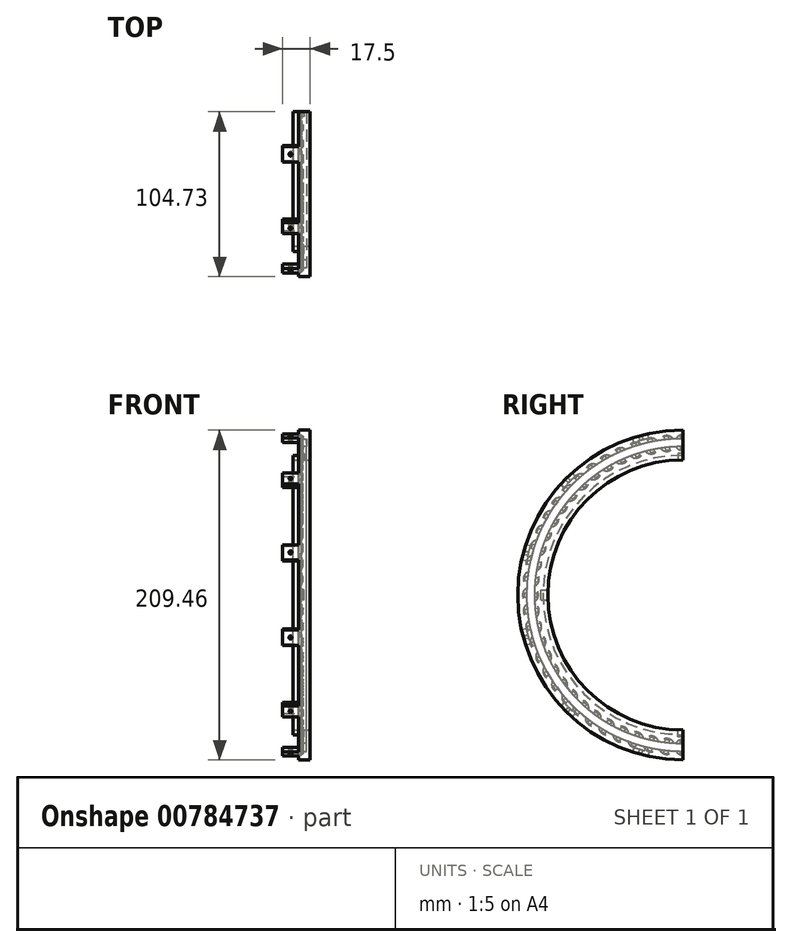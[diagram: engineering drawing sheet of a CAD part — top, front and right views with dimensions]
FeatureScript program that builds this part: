
annotation { "Feature Type Name" : "Feature", "Feature Type Description" : "" }
export const myFeature = defineFeature(function(context is Context, id is Id, definition is map)
    precondition{}
    {
        {
            var Q0;
            Q0=qCreatedBy(makeId("Front.planeOp"),FACE);
            var sketch = newSketch(context, id + "F0", { "sketchPlane" : qUnion([Q0])});
            skLineSegment(sketch, "E0.bottom", {"start": v(-125, 105) * mm, "end": v(125, 105) * mm, "construction": true});
            skLineSegment(sketch, "E0.top", {"start": v(-125, -105) * mm, "end": v(125, -105) * mm, "construction": true});
            skLineSegment(sketch, "E0.left", {"start": v(-125, 105) * mm, "end": v(-125, -105) * mm, "construction": true});
            skLineSegment(sketch, "E0.right", {"start": v(125, 105) * mm, "end": v(125, -105) * mm, "construction": true});
            skLineSegment(sketch, "E1", {"start": v(-16.75, 85.73) * mm, "end": v(-16.75, 88.73) * mm});
            skLineSegment(sketch, "E2", {"start": v(-16.75, 88.73) * mm, "end": v(-13.25, 88.73) * mm});
            skLineSegment(sketch, "E3", {"start": v(-16.75, 85.73) * mm, "end": v(-5.75, 85.73) * mm});
            skLineSegment(sketch, "E4", {"start": v(-5.75, 85.73) * mm, "end": v(-5.75, 104.73) * mm});
            skLineSegment(sketch, "E5", {"start": v(-13.25, 104.73) * mm, "end": v(-13.25, 99.23) * mm});
            skLineSegment(sketch, "E6", {"start": v(-13.25, 99.23) * mm, "end": v(-8.25, 99.23) * mm});
            skLineSegment(sketch, "E7", {"start": v(-8.25, 99.23) * mm, "end": v(-8.25, 94.23) * mm});
            skLineSegment(sketch, "E8", {"start": v(-8.25, 94.23) * mm, "end": v(-13.25, 94.23) * mm});
            skLineSegment(sketch, "E9.trimOffspring", {"start": v(-13.25, 94.23) * mm, "end": v(-13.25, 88.73) * mm});
            skLineSegment(sketch, "E10", {"start": v(-74.95, 0) * mm, "end": v(74.95, 0) * mm});
            skLineSegment(sketch, "E11", {"start": v(-13.25, 104.73) * mm, "end": v(-8.75, 104.73) * mm});
            skLineSegment(sketch, "E12.trimOffspring", {"start": v(-7.75, 104.73) * mm, "end": v(-5.75, 104.73) * mm});
            skLineSegment(sketch, "E13", {"start": v(-7.75, 104.73) * mm, "end": v(-8.75, 104.73) * mm});
            skSolve(sketch);
        }
        {
            var Q0;
            Q0 = qSketchRegion(id + "F0", true);
            var Q1;
            Q1=sQuery(id+"F0.wireOp",EDGE,"E10");
            revolve(context, id + "F1", {"surfaceOperationType" : NewSurfaceOperationType.NEW, "entities" : qUnion([Q0]), "axis" : qUnion([Q1]), "revolveType" : RevolveType.ONE_DIRECTION, "angle" : 180 * degree});
        }
        {
            var Q0;
            Q0=qCreatedBy(makeId("Top.planeOp"),FACE);
            cPlane(context, id + "F2", {"entities" : qUnion([Q0]), "cplaneType" : CPlaneType.OFFSET, "offset" : 80 * mm, "oppositeDirection" : true, "width" : 150 * mm, "height" : 150 * mm});
        }
        {
            var Q0;
            Q0=qCreatedBy(id+"F2.planeOp",FACE);
            var sketch = newSketch(context, id + "F3", { "sketchPlane" : qUnion([Q0])});
            skLineSegment(sketch, "E14.top", {"start": v(-9.65, -3.1) * mm, "end": v(-12.85, -3.1) * mm});
            skLineSegment(sketch, "E14.left", {"start": v(-9.65, 0) * mm, "end": v(-9.65, -3.1) * mm});
            skLineSegment(sketch, "E14.right", {"start": v(-12.85, 0) * mm, "end": v(-12.85, -3.1) * mm});
            skLineSegment(sketch, "E15.top", {"start": v(-9.65, 1.57) * mm, "end": v(-12.85, 1.57) * mm});
            skLineSegment(sketch, "E15.left", {"start": v(-9.65, 0) * mm, "end": v(-9.65, 1.57) * mm});
            skLineSegment(sketch, "E15.right", {"start": v(-12.85, 0) * mm, "end": v(-12.85, 1.57) * mm});
            skSolve(sketch);
        }
        {
            var Q0;
            Q0 = qSketchRegion(id + "F3", true);
            var Q1;
            Q1=makeQuery(id+"F1.opRevolve","SWEPT_FACE",FACE,{"disambiguationData":[OSD([sQuery(id+"F0.wireOp",EDGE,"E2")])]});
            extrude(context, id + "F4", {"entities" : qUnion([Q0]), "operationType" : NewBodyOperationType.REMOVE, "oppositeDirection" : true, "depth" : 10 * mm, "endBoundEntityFace" : qUnion([Q1]), "offsetDistance" : 25 * mm});
        }
        {
            var Q0;
            Q0=qCreatedBy(makeId("Front.planeOp"),FACE);
            cPlane(context, id + "F5", {"entities" : qUnion([Q0]), "cplaneType" : CPlaneType.OFFSET, "offset" : 80 * mm, "width" : 150 * mm, "height" : 150 * mm});
        }
        {
            var Q0;
            Q0=qCreatedBy(makeId("Top.planeOp"),FACE);
            cPlane(context, id + "F6", {"entities" : qUnion([Q0]), "cplaneType" : CPlaneType.OFFSET, "offset" : 80 * mm, "width" : 150 * mm, "height" : 150 * mm});
        }
        {
            var Q0;
            Q0=qCreatedBy(id+"F5.planeOp",FACE);
            var sketch = newSketch(context, id + "F7", { "sketchPlane" : qUnion([Q0])});
            skLineSegment(sketch, "E16.bottom", {"start": v(-9.65, -3.1) * mm, "end": v(-12.85, -3.1) * mm});
            skLineSegment(sketch, "E16.top", {"start": v(-9.65, 3.1) * mm, "end": v(-12.85, 3.1) * mm});
            skLineSegment(sketch, "E16.left", {"start": v(-9.65, -3.1) * mm, "end": v(-9.65, 3.1) * mm});
            skLineSegment(sketch, "E16.right", {"start": v(-12.85, -3.1) * mm, "end": v(-12.85, 3.1) * mm});
            skSolve(sketch);
        }
        {
            var Q0;
            Q0 = qSketchRegion(id + "F7", true);
            var Q1;
            Q1=makeQuery(id+"F1.opRevolve","SWEPT_FACE",FACE,{"disambiguationData":[OSD([sQuery(id+"F0.wireOp",EDGE,"E2")])]});
            extrude(context, id + "F8", {"entities" : qUnion([Q0]), "operationType" : NewBodyOperationType.REMOVE, "depth" : 10 * mm, "endBoundEntityFace" : qUnion([Q1]), "offsetDistance" : 25 * mm});
        }
        {
            var Q0;
            Q0=qCreatedBy(id+"F6.planeOp",FACE);
            var sketch = newSketch(context, id + "F9", { "sketchPlane" : qUnion([Q0])});
            skLineSegment(sketch, "E17.bottom", {"start": v(-9.65, 0) * mm, "end": v(-12.85, 0) * mm});
            skLineSegment(sketch, "E17.top", {"start": v(-9.65, -3.1) * mm, "end": v(-12.85, -3.1) * mm});
            skLineSegment(sketch, "E17.left", {"start": v(-9.65, 0) * mm, "end": v(-9.65, -3.1) * mm});
            skLineSegment(sketch, "E17.right", {"start": v(-12.85, 0) * mm, "end": v(-12.85, -3.1) * mm});
            skSolve(sketch);
        }
        {
            var Q0;
            Q0 = qSketchRegion(id + "F9", true);
            var Q1;
            Q1=makeQuery(id+"F1.opRevolve","SWEPT_FACE",FACE,{"disambiguationData":[OSD([sQuery(id+"F0.wireOp",EDGE,"E2")])]});
            extrude(context, id + "F10", {"entities" : qUnion([Q0]), "operationType" : NewBodyOperationType.REMOVE, "depth" : 10 * mm, "endBoundEntityFace" : qUnion([Q1]), "offsetDistance" : 25 * mm});
        }
        {
            var Q0;
            Q0=makeQuery(id+"F1.opRevolve","SWEPT_FACE",FACE,{"disambiguationData":[OSD([sQuery(id+"F0.wireOp",EDGE,"E7")])]});
            var sketch = newSketch(context, id + "F11", { "sketchPlane" : qUnion([Q0])});
            skCircle(sketch, "E18", {"center": v(0, 96.73) * mm, "radius": 5 * mm});
            skCircle(sketch, "E19.1.0", {"center": v(-10.11, 96.2) * mm, "radius": 5 * mm});
            skCircle(sketch, "E19.2.0", {"center": v(-20.11, 94.62) * mm, "radius": 5 * mm});
            skCircle(sketch, "E19.3.0", {"center": v(-29.9, 92) * mm, "radius": 5 * mm});
            skCircle(sketch, "E19.4.0", {"center": v(-39.34, 88.37) * mm, "radius": 5 * mm});
            skCircle(sketch, "E19.5.0", {"center": v(-48.36, 83.77) * mm, "radius": 5 * mm});
            skCircle(sketch, "E19.6.0", {"center": v(-56.86, 78.26) * mm, "radius": 5 * mm});
            skCircle(sketch, "E19.7.0", {"center": v(-64.73, 71.88) * mm, "radius": 5 * mm});
            skCircle(sketch, "E19.8.0", {"center": v(-71.88, 64.73) * mm, "radius": 5 * mm});
            skCircle(sketch, "E19.9.0", {"center": v(-78.26, 56.86) * mm, "radius": 5 * mm});
            skCircle(sketch, "E19.10.0", {"center": v(-83.77, 48.36) * mm, "radius": 5 * mm});
            skCircle(sketch, "E19.11.0", {"center": v(-88.37, 39.34) * mm, "radius": 5 * mm});
            skCircle(sketch, "E19.12.0", {"center": v(-92, 29.9) * mm, "radius": 5 * mm});
            skCircle(sketch, "E19.13.0", {"center": v(-94.62, 20.11) * mm, "radius": 5 * mm});
            skCircle(sketch, "E19.14.0", {"center": v(-96.2, 10.11) * mm, "radius": 5 * mm});
            skCircle(sketch, "E19.15.0", {"center": v(-96.73, 0) * mm, "radius": 5 * mm});
            skCircle(sketch, "E19.16.0", {"center": v(-96.2, -10.11) * mm, "radius": 5 * mm});
            skCircle(sketch, "E19.17.0", {"center": v(-94.62, -20.11) * mm, "radius": 5 * mm});
            skCircle(sketch, "E19.18.0", {"center": v(-92, -29.9) * mm, "radius": 5 * mm});
            skCircle(sketch, "E19.19.0", {"center": v(-88.37, -39.34) * mm, "radius": 5 * mm});
            skCircle(sketch, "E19.20.0", {"center": v(-83.77, -48.36) * mm, "radius": 5 * mm});
            skCircle(sketch, "E19.21.0", {"center": v(-78.26, -56.86) * mm, "radius": 5 * mm});
            skCircle(sketch, "E19.22.0", {"center": v(-71.88, -64.73) * mm, "radius": 5 * mm});
            skCircle(sketch, "E19.23.0", {"center": v(-64.73, -71.88) * mm, "radius": 5 * mm});
            skCircle(sketch, "E19.24.0", {"center": v(-56.86, -78.26) * mm, "radius": 5 * mm});
            skCircle(sketch, "E19.25.0", {"center": v(-48.36, -83.77) * mm, "radius": 5 * mm});
            skCircle(sketch, "E19.26.0", {"center": v(-39.34, -88.37) * mm, "radius": 5 * mm});
            skCircle(sketch, "E19.27.0", {"center": v(-29.9, -92) * mm, "radius": 5 * mm});
            skCircle(sketch, "E19.28.0", {"center": v(-20.11, -94.62) * mm, "radius": 5 * mm});
            skCircle(sketch, "E19.29.0", {"center": v(-10.11, -96.2) * mm, "radius": 5 * mm});
            skCircle(sketch, "E19.30.0", {"center": v(0, -96.73) * mm, "radius": 5 * mm});
            skCircle(sketch, "E19.31.0", {"center": v(10.11, -96.2) * mm, "radius": 5 * mm});
            skCircle(sketch, "E19.32.0", {"center": v(20.11, -94.62) * mm, "radius": 5 * mm});
            skCircle(sketch, "E19.33.0", {"center": v(29.9, -92) * mm, "radius": 5 * mm});
            skCircle(sketch, "E19.34.0", {"center": v(39.34, -88.37) * mm, "radius": 5 * mm});
            skCircle(sketch, "E19.35.0", {"center": v(48.36, -83.77) * mm, "radius": 5 * mm});
            skCircle(sketch, "E19.36.0", {"center": v(56.86, -78.26) * mm, "radius": 5 * mm});
            skCircle(sketch, "E19.37.0", {"center": v(64.73, -71.88) * mm, "radius": 5 * mm});
            skCircle(sketch, "E19.38.0", {"center": v(71.88, -64.73) * mm, "radius": 5 * mm});
            skCircle(sketch, "E19.39.0", {"center": v(78.26, -56.86) * mm, "radius": 5 * mm});
            skCircle(sketch, "E19.40.0", {"center": v(83.77, -48.37) * mm, "radius": 5 * mm});
            skCircle(sketch, "E19.41.0", {"center": v(88.37, -39.34) * mm, "radius": 5 * mm});
            skCircle(sketch, "E19.42.0", {"center": v(92, -29.9) * mm, "radius": 5 * mm});
            skCircle(sketch, "E19.43.0", {"center": v(94.62, -20.11) * mm, "radius": 5 * mm});
            skCircle(sketch, "E19.44.0", {"center": v(96.2, -10.11) * mm, "radius": 5 * mm});
            skCircle(sketch, "E19.45.0", {"center": v(96.73, 0) * mm, "radius": 5 * mm});
            skCircle(sketch, "E19.46.0", {"center": v(96.2, 10.11) * mm, "radius": 5 * mm});
            skCircle(sketch, "E19.47.0", {"center": v(94.62, 20.11) * mm, "radius": 5 * mm});
            skCircle(sketch, "E19.48.0", {"center": v(92, 29.9) * mm, "radius": 5 * mm});
            skCircle(sketch, "E19.49.0", {"center": v(88.37, 39.34) * mm, "radius": 5 * mm});
            skCircle(sketch, "E19.50.0", {"center": v(83.77, 48.36) * mm, "radius": 5 * mm});
            skCircle(sketch, "E19.51.0", {"center": v(78.26, 56.86) * mm, "radius": 5 * mm});
            skCircle(sketch, "E19.52.0", {"center": v(71.88, 64.73) * mm, "radius": 5 * mm});
            skCircle(sketch, "E19.53.0", {"center": v(64.73, 71.88) * mm, "radius": 5 * mm});
            skCircle(sketch, "E19.54.0", {"center": v(56.86, 78.26) * mm, "radius": 5 * mm});
            skCircle(sketch, "E19.55.0", {"center": v(48.36, 83.77) * mm, "radius": 5 * mm});
            skCircle(sketch, "E19.56.0", {"center": v(39.34, 88.37) * mm, "radius": 5 * mm});
            skCircle(sketch, "E19.57.0", {"center": v(29.9, 92) * mm, "radius": 5 * mm});
            skCircle(sketch, "E19.58.0", {"center": v(20.11, 94.62) * mm, "radius": 5 * mm});
            skCircle(sketch, "E19.59.0", {"center": v(10.11, 96.2) * mm, "radius": 5 * mm});
            skPoint(sketch, "E19.center", {"position": v(0, 0) * mm});
            skSolve(sketch);
        }
        {
            var Q0;
            Q0 = qSketchRegion(id + "F11", true);
            extrude(context, id + "F12", {"entities" : qUnion([Q0]), "operationType" : NewBodyOperationType.REMOVE, "depth" : 25 * mm, "offsetDistance" : 25 * mm, "hasSecondDirection" : true, "secondDirectionOppositeDirection" : false, "secondDirectionDepth" : 3 * mm});
        }
        {
            var Q0;
            Q0=makeQuery(id+"F1.opRevolve","SWEPT_FACE",FACE,{"disambiguationData":[OSD([sQuery(id+"F0.wireOp",EDGE,"E7")])]});
            var sketch = newSketch(context, id + "F13", { "sketchPlane" : qUnion([Q0])});
            skLineSegment(sketch, "E20.bottom", {"start": v(1.36, 92.48) * mm, "end": v(0, 92.48) * mm});
            skLineSegment(sketch, "E20.top", {"start": v(1.36, 100.98) * mm, "end": v(0, 100.98) * mm});
            skLineSegment(sketch, "E20.left", {"start": v(1.36, 92.48) * mm, "end": v(1.36, 100.98) * mm});
            skLineSegment(sketch, "E21", {"start": v(1.96, 96.73) * mm, "end": v(-1.46, 96.73) * mm, "construction": true});
            skLineSegment(sketch, "E22.MirrorCS", {"start": v(-1.36, 92.48) * mm, "end": v(0, 92.48) * mm});
            skLineSegment(sketch, "E23.MirrorCS", {"start": v(-1.36, 92.48) * mm, "end": v(-1.36, 100.98) * mm});
            skLineSegment(sketch, "E24.MirrorCS", {"start": v(-1.36, 100.98) * mm, "end": v(0, 100.98) * mm});
            skLineSegment(sketch, "E25", {"start": v(0, 92.48) * mm, "end": v(0, 100.98) * mm, "construction": true});
            skLineSegment(sketch, "E26.1.0", {"start": v(-8.32, 92.12) * mm, "end": v(-9.67, 91.97) * mm});
            skLineSegment(sketch, "E26.1.1", {"start": v(-9.2, 100.57) * mm, "end": v(-10.56, 100.43) * mm});
            skLineSegment(sketch, "E26.1.2", {"start": v(-8.32, 92.12) * mm, "end": v(-9.2, 100.57) * mm});
            skLineSegment(sketch, "E26.1.3", {"start": v(-8.16, 96.4) * mm, "end": v(-11.56, 96.05) * mm, "construction": true});
            skLineSegment(sketch, "E26.1.4", {"start": v(-11.02, 91.83) * mm, "end": v(-9.67, 91.97) * mm});
            skLineSegment(sketch, "E26.1.5", {"start": v(-11.02, 91.83) * mm, "end": v(-11.9, 100.28) * mm});
            skLineSegment(sketch, "E26.1.6", {"start": v(-11.9, 100.28) * mm, "end": v(-10.56, 100.43) * mm});
            skLineSegment(sketch, "E26.1.7", {"start": v(-9.67, 91.97) * mm, "end": v(-10.56, 100.43) * mm, "construction": true});
            skLineSegment(sketch, "E26.2.0", {"start": v(-17.9, 90.74) * mm, "end": v(-19.23, 90.46) * mm});
            skLineSegment(sketch, "E26.2.1", {"start": v(-19.67, 99.06) * mm, "end": v(-21, 98.77) * mm});
            skLineSegment(sketch, "E26.2.2", {"start": v(-17.9, 90.74) * mm, "end": v(-19.67, 99.06) * mm});
            skLineSegment(sketch, "E26.2.3", {"start": v(-18.2, 95.02) * mm, "end": v(-21.54, 94.31) * mm, "construction": true});
            skLineSegment(sketch, "E26.2.4", {"start": v(-20.56, 90.18) * mm, "end": v(-19.23, 90.46) * mm});
            skLineSegment(sketch, "E26.2.5", {"start": v(-20.56, 90.18) * mm, "end": v(-22.32, 98.5) * mm});
            skLineSegment(sketch, "E26.2.6", {"start": v(-22.32, 98.5) * mm, "end": v(-21, 98.77) * mm});
            skLineSegment(sketch, "E26.2.7", {"start": v(-19.23, 90.46) * mm, "end": v(-21, 98.77) * mm, "construction": true});
            skLineSegment(sketch, "E26.3.0", {"start": v(-27.29, 88.37) * mm, "end": v(-28.58, 87.95) * mm});
            skLineSegment(sketch, "E26.3.1", {"start": v(-29.91, 96.46) * mm, "end": v(-31.2, 96.04) * mm});
            skLineSegment(sketch, "E26.3.2", {"start": v(-27.29, 88.37) * mm, "end": v(-29.91, 96.46) * mm});
            skLineSegment(sketch, "E26.3.3", {"start": v(-28.02, 92.6) * mm, "end": v(-31.28, 91.54) * mm, "construction": true});
            skLineSegment(sketch, "E26.3.4", {"start": v(-29.87, 87.53) * mm, "end": v(-28.58, 87.95) * mm});
            skLineSegment(sketch, "E26.3.5", {"start": v(-29.87, 87.53) * mm, "end": v(-32.5, 95.62) * mm});
            skLineSegment(sketch, "E26.3.6", {"start": v(-32.5, 95.62) * mm, "end": v(-31.2, 96.04) * mm});
            skLineSegment(sketch, "E26.3.7", {"start": v(-28.58, 87.95) * mm, "end": v(-31.2, 96.04) * mm, "construction": true});
            skLineSegment(sketch, "E26.4.0", {"start": v(-36.37, 85.04) * mm, "end": v(-37.62, 84.48) * mm});
            skLineSegment(sketch, "E26.4.1", {"start": v(-39.83, 92.8) * mm, "end": v(-41.07, 92.25) * mm});
            skLineSegment(sketch, "E26.4.2", {"start": v(-36.37, 85.04) * mm, "end": v(-39.83, 92.8) * mm});
            skLineSegment(sketch, "E26.4.3", {"start": v(-37.55, 89.17) * mm, "end": v(-40.68, 87.77) * mm, "construction": true});
            skLineSegment(sketch, "E26.4.4", {"start": v(-38.86, 83.93) * mm, "end": v(-37.62, 84.48) * mm});
            skLineSegment(sketch, "E26.4.5", {"start": v(-38.86, 83.93) * mm, "end": v(-42.31, 91.7) * mm});
            skLineSegment(sketch, "E26.4.6", {"start": v(-42.31, 91.7) * mm, "end": v(-41.07, 92.25) * mm});
            skLineSegment(sketch, "E26.4.7", {"start": v(-37.62, 84.48) * mm, "end": v(-41.07, 92.25) * mm, "construction": true});
            skLineSegment(sketch, "E26.5.0", {"start": v(-45.06, 80.77) * mm, "end": v(-46.24, 80.1) * mm});
            skLineSegment(sketch, "E26.5.1", {"start": v(-49.31, 88.13) * mm, "end": v(-50.49, 87.45) * mm});
            skLineSegment(sketch, "E26.5.2", {"start": v(-45.06, 80.77) * mm, "end": v(-49.31, 88.13) * mm});
            skLineSegment(sketch, "E26.5.3", {"start": v(-46.67, 84.75) * mm, "end": v(-49.63, 83.04) * mm, "construction": true});
            skLineSegment(sketch, "E26.5.4", {"start": v(-47.42, 79.41) * mm, "end": v(-46.24, 80.1) * mm});
            skLineSegment(sketch, "E26.5.5", {"start": v(-47.42, 79.41) * mm, "end": v(-51.67, 86.77) * mm});
            skLineSegment(sketch, "E26.5.6", {"start": v(-51.67, 86.77) * mm, "end": v(-50.49, 87.45) * mm});
            skLineSegment(sketch, "E26.5.7", {"start": v(-46.24, 80.1) * mm, "end": v(-50.49, 87.45) * mm, "construction": true});
            skLineSegment(sketch, "E26.6.0", {"start": v(-53.26, 75.62) * mm, "end": v(-54.36, 74.82) * mm});
            skLineSegment(sketch, "E26.6.1", {"start": v(-58.26, 82.5) * mm, "end": v(-59.35, 81.7) * mm});
            skLineSegment(sketch, "E26.6.2", {"start": v(-53.26, 75.62) * mm, "end": v(-58.26, 82.5) * mm});
            skLineSegment(sketch, "E26.6.3", {"start": v(-55.27, 79.4) * mm, "end": v(-58.04, 77.4) * mm, "construction": true});
            skLineSegment(sketch, "E26.6.4", {"start": v(-55.46, 74.02) * mm, "end": v(-54.36, 74.82) * mm});
            skLineSegment(sketch, "E26.6.5", {"start": v(-55.46, 74.02) * mm, "end": v(-60.45, 80.9) * mm});
            skLineSegment(sketch, "E26.6.6", {"start": v(-60.45, 80.9) * mm, "end": v(-59.35, 81.7) * mm});
            skLineSegment(sketch, "E26.6.7", {"start": v(-54.36, 74.82) * mm, "end": v(-59.35, 81.7) * mm, "construction": true});
            skLineSegment(sketch, "E26.7.0", {"start": v(-60.87, 69.63) * mm, "end": v(-61.88, 68.73) * mm});
            skLineSegment(sketch, "E26.7.1", {"start": v(-66.56, 75.95) * mm, "end": v(-67.57, 75.04) * mm});
            skLineSegment(sketch, "E26.7.2", {"start": v(-60.87, 69.63) * mm, "end": v(-66.56, 75.95) * mm});
            skLineSegment(sketch, "E26.7.3", {"start": v(-63.27, 73.2) * mm, "end": v(-65.8, 70.9) * mm, "construction": true});
            skLineSegment(sketch, "E26.7.4", {"start": v(-62.9, 67.82) * mm, "end": v(-61.88, 68.73) * mm});
            skLineSegment(sketch, "E26.7.5", {"start": v(-62.9, 67.82) * mm, "end": v(-68.58, 74.13) * mm});
            skLineSegment(sketch, "E26.7.6", {"start": v(-68.58, 74.13) * mm, "end": v(-67.57, 75.04) * mm});
            skLineSegment(sketch, "E26.7.7", {"start": v(-61.88, 68.73) * mm, "end": v(-67.57, 75.04) * mm, "construction": true});
            skLineSegment(sketch, "E26.8.0", {"start": v(-67.82, 62.9) * mm, "end": v(-68.73, 61.88) * mm});
            skLineSegment(sketch, "E26.8.1", {"start": v(-74.13, 68.58) * mm, "end": v(-75.04, 67.57) * mm});
            skLineSegment(sketch, "E26.8.2", {"start": v(-67.82, 62.9) * mm, "end": v(-74.13, 68.58) * mm});
            skLineSegment(sketch, "E26.8.3", {"start": v(-70.57, 66.18) * mm, "end": v(-72.86, 63.64) * mm, "construction": true});
            skLineSegment(sketch, "E26.8.4", {"start": v(-69.63, 60.87) * mm, "end": v(-68.73, 61.88) * mm});
            skLineSegment(sketch, "E26.8.5", {"start": v(-69.63, 60.87) * mm, "end": v(-75.95, 66.56) * mm});
            skLineSegment(sketch, "E26.8.6", {"start": v(-75.95, 66.56) * mm, "end": v(-75.04, 67.57) * mm});
            skLineSegment(sketch, "E26.8.7", {"start": v(-68.73, 61.88) * mm, "end": v(-75.04, 67.57) * mm, "construction": true});
            skLineSegment(sketch, "E26.9.0", {"start": v(-74.02, 55.46) * mm, "end": v(-74.82, 54.36) * mm});
            skLineSegment(sketch, "E26.9.1", {"start": v(-80.9, 60.45) * mm, "end": v(-81.7, 59.35) * mm});
            skLineSegment(sketch, "E26.9.2", {"start": v(-74.02, 55.46) * mm, "end": v(-80.9, 60.45) * mm});
            skLineSegment(sketch, "E26.9.3", {"start": v(-77.1, 58.44) * mm, "end": v(-79.11, 55.68) * mm, "construction": true});
            skLineSegment(sketch, "E26.9.4", {"start": v(-75.62, 53.26) * mm, "end": v(-74.82, 54.36) * mm});
            skLineSegment(sketch, "E26.9.5", {"start": v(-75.62, 53.26) * mm, "end": v(-82.5, 58.26) * mm});
            skLineSegment(sketch, "E26.9.6", {"start": v(-82.5, 58.26) * mm, "end": v(-81.7, 59.35) * mm});
            skLineSegment(sketch, "E26.9.7", {"start": v(-74.82, 54.36) * mm, "end": v(-81.7, 59.35) * mm, "construction": true});
            skLineSegment(sketch, "E26.10.0", {"start": v(-79.41, 47.42) * mm, "end": v(-80.1, 46.24) * mm});
            skLineSegment(sketch, "E26.10.1", {"start": v(-86.77, 51.67) * mm, "end": v(-87.45, 50.49) * mm});
            skLineSegment(sketch, "E26.10.2", {"start": v(-79.41, 47.42) * mm, "end": v(-86.77, 51.67) * mm});
            skLineSegment(sketch, "E26.10.3", {"start": v(-82.79, 50.06) * mm, "end": v(-84.5, 47.1) * mm, "construction": true});
            skLineSegment(sketch, "E26.10.4", {"start": v(-80.77, 45.06) * mm, "end": v(-80.1, 46.24) * mm});
            skLineSegment(sketch, "E26.10.5", {"start": v(-80.77, 45.06) * mm, "end": v(-88.13, 49.31) * mm});
            skLineSegment(sketch, "E26.10.6", {"start": v(-88.13, 49.31) * mm, "end": v(-87.45, 50.49) * mm});
            skLineSegment(sketch, "E26.10.7", {"start": v(-80.1, 46.24) * mm, "end": v(-87.45, 50.49) * mm, "construction": true});
            skLineSegment(sketch, "E26.11.0", {"start": v(-83.93, 38.86) * mm, "end": v(-84.48, 37.62) * mm});
            skLineSegment(sketch, "E26.11.1", {"start": v(-91.7, 42.31) * mm, "end": v(-92.25, 41.07) * mm});
            skLineSegment(sketch, "E26.11.2", {"start": v(-83.93, 38.86) * mm, "end": v(-91.7, 42.31) * mm});
            skLineSegment(sketch, "E26.11.3", {"start": v(-87.57, 41.14) * mm, "end": v(-88.96, 38) * mm, "construction": true});
            skLineSegment(sketch, "E26.11.4", {"start": v(-85.04, 36.37) * mm, "end": v(-84.48, 37.62) * mm});
            skLineSegment(sketch, "E26.11.5", {"start": v(-85.04, 36.37) * mm, "end": v(-92.8, 39.83) * mm});
            skLineSegment(sketch, "E26.11.6", {"start": v(-92.8, 39.83) * mm, "end": v(-92.25, 41.07) * mm});
            skLineSegment(sketch, "E26.11.7", {"start": v(-84.48, 37.62) * mm, "end": v(-92.25, 41.07) * mm, "construction": true});
            skLineSegment(sketch, "E26.12.0", {"start": v(-87.53, 29.87) * mm, "end": v(-87.95, 28.58) * mm});
            skLineSegment(sketch, "E26.12.1", {"start": v(-95.62, 32.5) * mm, "end": v(-96.04, 31.2) * mm});
            skLineSegment(sketch, "E26.12.2", {"start": v(-87.53, 29.87) * mm, "end": v(-95.62, 32.5) * mm});
            skLineSegment(sketch, "E26.12.3", {"start": v(-91.39, 31.76) * mm, "end": v(-92.45, 28.5) * mm, "construction": true});
            skLineSegment(sketch, "E26.12.4", {"start": v(-88.37, 27.29) * mm, "end": v(-87.95, 28.58) * mm});
            skLineSegment(sketch, "E26.12.5", {"start": v(-88.37, 27.29) * mm, "end": v(-96.46, 29.91) * mm});
            skLineSegment(sketch, "E26.12.6", {"start": v(-96.46, 29.91) * mm, "end": v(-96.04, 31.2) * mm});
            skLineSegment(sketch, "E26.12.7", {"start": v(-87.95, 28.58) * mm, "end": v(-96.04, 31.2) * mm, "construction": true});
            skLineSegment(sketch, "E26.13.0", {"start": v(-90.18, 20.56) * mm, "end": v(-90.46, 19.23) * mm});
            skLineSegment(sketch, "E26.13.1", {"start": v(-98.5, 22.32) * mm, "end": v(-98.77, 21) * mm});
            skLineSegment(sketch, "E26.13.2", {"start": v(-90.18, 20.56) * mm, "end": v(-98.5, 22.32) * mm});
            skLineSegment(sketch, "E26.13.3", {"start": v(-94.2, 22.03) * mm, "end": v(-94.92, 18.68) * mm, "construction": true});
            skLineSegment(sketch, "E26.13.4", {"start": v(-90.74, 17.9) * mm, "end": v(-90.46, 19.23) * mm});
            skLineSegment(sketch, "E26.13.5", {"start": v(-90.74, 17.9) * mm, "end": v(-99.06, 19.67) * mm});
            skLineSegment(sketch, "E26.13.6", {"start": v(-99.06, 19.67) * mm, "end": v(-98.77, 21) * mm});
            skLineSegment(sketch, "E26.13.7", {"start": v(-90.46, 19.23) * mm, "end": v(-98.77, 21) * mm, "construction": true});
            skLineSegment(sketch, "E26.14.0", {"start": v(-91.83, 11.02) * mm, "end": v(-91.97, 9.67) * mm});
            skLineSegment(sketch, "E26.14.1", {"start": v(-100.28, 11.9) * mm, "end": v(-100.43, 10.56) * mm});
            skLineSegment(sketch, "E26.14.2", {"start": v(-91.83, 11.02) * mm, "end": v(-100.28, 11.9) * mm});
            skLineSegment(sketch, "E26.14.3", {"start": v(-96, 12.06) * mm, "end": v(-96.35, 8.66) * mm, "construction": true});
            skLineSegment(sketch, "E26.14.4", {"start": v(-92.12, 8.32) * mm, "end": v(-91.97, 9.67) * mm});
            skLineSegment(sketch, "E26.14.5", {"start": v(-92.12, 8.32) * mm, "end": v(-100.57, 9.2) * mm});
            skLineSegment(sketch, "E26.14.6", {"start": v(-100.57, 9.2) * mm, "end": v(-100.43, 10.56) * mm});
            skLineSegment(sketch, "E26.14.7", {"start": v(-91.97, 9.67) * mm, "end": v(-100.43, 10.56) * mm, "construction": true});
            skLineSegment(sketch, "E26.15.0", {"start": v(-92.48, 1.36) * mm, "end": v(-92.48, 0) * mm});
            skLineSegment(sketch, "E26.15.1", {"start": v(-100.98, 1.36) * mm, "end": v(-100.98, 0) * mm});
            skLineSegment(sketch, "E26.15.2", {"start": v(-92.48, 1.36) * mm, "end": v(-100.98, 1.36) * mm});
            skLineSegment(sketch, "E26.15.3", {"start": v(-96.73, 1.96) * mm, "end": v(-96.73, -1.46) * mm, "construction": true});
            skLineSegment(sketch, "E26.15.4", {"start": v(-92.48, -1.36) * mm, "end": v(-92.48, 0) * mm});
            skLineSegment(sketch, "E26.15.5", {"start": v(-92.48, -1.36) * mm, "end": v(-100.98, -1.36) * mm});
            skLineSegment(sketch, "E26.15.6", {"start": v(-100.98, -1.36) * mm, "end": v(-100.98, 0) * mm});
            skLineSegment(sketch, "E26.15.7", {"start": v(-92.48, 0) * mm, "end": v(-100.98, 0) * mm, "construction": true});
            skLineSegment(sketch, "E26.16.0", {"start": v(-92.12, -8.32) * mm, "end": v(-91.97, -9.67) * mm});
            skLineSegment(sketch, "E26.16.1", {"start": v(-100.57, -9.2) * mm, "end": v(-100.43, -10.56) * mm});
            skLineSegment(sketch, "E26.16.2", {"start": v(-92.12, -8.32) * mm, "end": v(-100.57, -9.2) * mm});
            skLineSegment(sketch, "E26.16.3", {"start": v(-96.4, -8.16) * mm, "end": v(-96.05, -11.56) * mm, "construction": true});
            skLineSegment(sketch, "E26.16.4", {"start": v(-91.83, -11.02) * mm, "end": v(-91.97, -9.67) * mm});
            skLineSegment(sketch, "E26.16.5", {"start": v(-91.83, -11.02) * mm, "end": v(-100.28, -11.9) * mm});
            skLineSegment(sketch, "E26.16.6", {"start": v(-100.28, -11.9) * mm, "end": v(-100.43, -10.56) * mm});
            skLineSegment(sketch, "E26.16.7", {"start": v(-91.97, -9.67) * mm, "end": v(-100.43, -10.56) * mm, "construction": true});
            skLineSegment(sketch, "E26.17.0", {"start": v(-90.74, -17.9) * mm, "end": v(-90.46, -19.23) * mm});
            skLineSegment(sketch, "E26.17.1", {"start": v(-99.06, -19.67) * mm, "end": v(-98.77, -21) * mm});
            skLineSegment(sketch, "E26.17.2", {"start": v(-90.74, -17.9) * mm, "end": v(-99.06, -19.67) * mm});
            skLineSegment(sketch, "E26.17.3", {"start": v(-95.02, -18.2) * mm, "end": v(-94.31, -21.54) * mm, "construction": true});
            skLineSegment(sketch, "E26.17.4", {"start": v(-90.18, -20.56) * mm, "end": v(-90.46, -19.23) * mm});
            skLineSegment(sketch, "E26.17.5", {"start": v(-90.18, -20.56) * mm, "end": v(-98.5, -22.32) * mm});
            skLineSegment(sketch, "E26.17.6", {"start": v(-98.5, -22.32) * mm, "end": v(-98.77, -21) * mm});
            skLineSegment(sketch, "E26.17.7", {"start": v(-90.46, -19.23) * mm, "end": v(-98.77, -21) * mm, "construction": true});
            skLineSegment(sketch, "E26.18.0", {"start": v(-88.37, -27.29) * mm, "end": v(-87.95, -28.58) * mm});
            skLineSegment(sketch, "E26.18.1", {"start": v(-96.46, -29.91) * mm, "end": v(-96.04, -31.2) * mm});
            skLineSegment(sketch, "E26.18.2", {"start": v(-88.37, -27.29) * mm, "end": v(-96.46, -29.91) * mm});
            skLineSegment(sketch, "E26.18.3", {"start": v(-92.6, -28.02) * mm, "end": v(-91.54, -31.28) * mm, "construction": true});
            skLineSegment(sketch, "E26.18.4", {"start": v(-87.53, -29.87) * mm, "end": v(-87.95, -28.58) * mm});
            skLineSegment(sketch, "E26.18.5", {"start": v(-87.53, -29.87) * mm, "end": v(-95.62, -32.5) * mm});
            skLineSegment(sketch, "E26.18.6", {"start": v(-95.62, -32.5) * mm, "end": v(-96.04, -31.2) * mm});
            skLineSegment(sketch, "E26.18.7", {"start": v(-87.95, -28.58) * mm, "end": v(-96.04, -31.2) * mm, "construction": true});
            skLineSegment(sketch, "E26.19.0", {"start": v(-85.04, -36.37) * mm, "end": v(-84.48, -37.62) * mm});
            skLineSegment(sketch, "E26.19.1", {"start": v(-92.8, -39.83) * mm, "end": v(-92.25, -41.07) * mm});
            skLineSegment(sketch, "E26.19.2", {"start": v(-85.04, -36.37) * mm, "end": v(-92.8, -39.83) * mm});
            skLineSegment(sketch, "E26.19.3", {"start": v(-89.17, -37.55) * mm, "end": v(-87.77, -40.68) * mm, "construction": true});
            skLineSegment(sketch, "E26.19.4", {"start": v(-83.93, -38.86) * mm, "end": v(-84.48, -37.62) * mm});
            skLineSegment(sketch, "E26.19.5", {"start": v(-83.93, -38.86) * mm, "end": v(-91.7, -42.31) * mm});
            skLineSegment(sketch, "E26.19.6", {"start": v(-91.7, -42.31) * mm, "end": v(-92.25, -41.07) * mm});
            skLineSegment(sketch, "E26.19.7", {"start": v(-84.48, -37.62) * mm, "end": v(-92.25, -41.07) * mm, "construction": true});
            skLineSegment(sketch, "E26.20.0", {"start": v(-80.77, -45.06) * mm, "end": v(-80.1, -46.24) * mm});
            skLineSegment(sketch, "E26.20.1", {"start": v(-88.13, -49.31) * mm, "end": v(-87.45, -50.49) * mm});
            skLineSegment(sketch, "E26.20.2", {"start": v(-80.77, -45.06) * mm, "end": v(-88.13, -49.31) * mm});
            skLineSegment(sketch, "E26.20.3", {"start": v(-84.75, -46.67) * mm, "end": v(-83.04, -49.63) * mm, "construction": true});
            skLineSegment(sketch, "E26.20.4", {"start": v(-79.41, -47.42) * mm, "end": v(-80.1, -46.24) * mm});
            skLineSegment(sketch, "E26.20.5", {"start": v(-79.41, -47.42) * mm, "end": v(-86.77, -51.67) * mm});
            skLineSegment(sketch, "E26.20.6", {"start": v(-86.77, -51.67) * mm, "end": v(-87.45, -50.49) * mm});
            skLineSegment(sketch, "E26.20.7", {"start": v(-80.1, -46.24) * mm, "end": v(-87.45, -50.49) * mm, "construction": true});
            skLineSegment(sketch, "E26.21.0", {"start": v(-75.62, -53.26) * mm, "end": v(-74.82, -54.36) * mm});
            skLineSegment(sketch, "E26.21.1", {"start": v(-82.5, -58.26) * mm, "end": v(-81.7, -59.35) * mm});
            skLineSegment(sketch, "E26.21.2", {"start": v(-75.62, -53.26) * mm, "end": v(-82.5, -58.26) * mm});
            skLineSegment(sketch, "E26.21.3", {"start": v(-79.4, -55.27) * mm, "end": v(-77.4, -58.04) * mm, "construction": true});
            skLineSegment(sketch, "E26.21.4", {"start": v(-74.02, -55.46) * mm, "end": v(-74.82, -54.36) * mm});
            skLineSegment(sketch, "E26.21.5", {"start": v(-74.02, -55.46) * mm, "end": v(-80.9, -60.45) * mm});
            skLineSegment(sketch, "E26.21.6", {"start": v(-80.9, -60.45) * mm, "end": v(-81.7, -59.35) * mm});
            skLineSegment(sketch, "E26.21.7", {"start": v(-74.82, -54.36) * mm, "end": v(-81.7, -59.35) * mm, "construction": true});
            skLineSegment(sketch, "E26.22.0", {"start": v(-69.63, -60.87) * mm, "end": v(-68.73, -61.88) * mm});
            skLineSegment(sketch, "E26.22.1", {"start": v(-75.95, -66.56) * mm, "end": v(-75.04, -67.57) * mm});
            skLineSegment(sketch, "E26.22.2", {"start": v(-69.63, -60.87) * mm, "end": v(-75.95, -66.56) * mm});
            skLineSegment(sketch, "E26.22.3", {"start": v(-73.2, -63.27) * mm, "end": v(-70.9, -65.8) * mm, "construction": true});
            skLineSegment(sketch, "E26.22.4", {"start": v(-67.82, -62.9) * mm, "end": v(-68.73, -61.88) * mm});
            skLineSegment(sketch, "E26.22.5", {"start": v(-67.82, -62.9) * mm, "end": v(-74.13, -68.58) * mm});
            skLineSegment(sketch, "E26.22.6", {"start": v(-74.13, -68.58) * mm, "end": v(-75.04, -67.57) * mm});
            skLineSegment(sketch, "E26.22.7", {"start": v(-68.73, -61.88) * mm, "end": v(-75.04, -67.57) * mm, "construction": true});
            skLineSegment(sketch, "E26.23.0", {"start": v(-62.9, -67.82) * mm, "end": v(-61.88, -68.73) * mm});
            skLineSegment(sketch, "E26.23.1", {"start": v(-68.58, -74.13) * mm, "end": v(-67.57, -75.04) * mm});
            skLineSegment(sketch, "E26.23.2", {"start": v(-62.9, -67.82) * mm, "end": v(-68.58, -74.13) * mm});
            skLineSegment(sketch, "E26.23.3", {"start": v(-66.18, -70.57) * mm, "end": v(-63.64, -72.86) * mm, "construction": true});
            skLineSegment(sketch, "E26.23.4", {"start": v(-60.87, -69.63) * mm, "end": v(-61.88, -68.73) * mm});
            skLineSegment(sketch, "E26.23.5", {"start": v(-60.87, -69.63) * mm, "end": v(-66.56, -75.95) * mm});
            skLineSegment(sketch, "E26.23.6", {"start": v(-66.56, -75.95) * mm, "end": v(-67.57, -75.04) * mm});
            skLineSegment(sketch, "E26.23.7", {"start": v(-61.88, -68.73) * mm, "end": v(-67.57, -75.04) * mm, "construction": true});
            skLineSegment(sketch, "E26.24.0", {"start": v(-55.46, -74.02) * mm, "end": v(-54.36, -74.82) * mm});
            skLineSegment(sketch, "E26.24.1", {"start": v(-60.45, -80.9) * mm, "end": v(-59.35, -81.7) * mm});
            skLineSegment(sketch, "E26.24.2", {"start": v(-55.46, -74.02) * mm, "end": v(-60.45, -80.9) * mm});
            skLineSegment(sketch, "E26.24.3", {"start": v(-58.44, -77.1) * mm, "end": v(-55.68, -79.11) * mm, "construction": true});
            skLineSegment(sketch, "E26.24.4", {"start": v(-53.26, -75.62) * mm, "end": v(-54.36, -74.82) * mm});
            skLineSegment(sketch, "E26.24.5", {"start": v(-53.26, -75.62) * mm, "end": v(-58.26, -82.5) * mm});
            skLineSegment(sketch, "E26.24.6", {"start": v(-58.26, -82.5) * mm, "end": v(-59.35, -81.7) * mm});
            skLineSegment(sketch, "E26.24.7", {"start": v(-54.36, -74.82) * mm, "end": v(-59.35, -81.7) * mm, "construction": true});
            skLineSegment(sketch, "E26.25.0", {"start": v(-47.42, -79.41) * mm, "end": v(-46.24, -80.1) * mm});
            skLineSegment(sketch, "E26.25.1", {"start": v(-51.67, -86.77) * mm, "end": v(-50.49, -87.45) * mm});
            skLineSegment(sketch, "E26.25.2", {"start": v(-47.42, -79.41) * mm, "end": v(-51.67, -86.77) * mm});
            skLineSegment(sketch, "E26.25.3", {"start": v(-50.06, -82.79) * mm, "end": v(-47.1, -84.5) * mm, "construction": true});
            skLineSegment(sketch, "E26.25.4", {"start": v(-45.06, -80.77) * mm, "end": v(-46.24, -80.1) * mm});
            skLineSegment(sketch, "E26.25.5", {"start": v(-45.06, -80.77) * mm, "end": v(-49.31, -88.13) * mm});
            skLineSegment(sketch, "E26.25.6", {"start": v(-49.31, -88.13) * mm, "end": v(-50.49, -87.45) * mm});
            skLineSegment(sketch, "E26.25.7", {"start": v(-46.24, -80.1) * mm, "end": v(-50.49, -87.45) * mm, "construction": true});
            skLineSegment(sketch, "E26.26.0", {"start": v(-38.86, -83.93) * mm, "end": v(-37.62, -84.48) * mm});
            skLineSegment(sketch, "E26.26.1", {"start": v(-42.31, -91.7) * mm, "end": v(-41.07, -92.25) * mm});
            skLineSegment(sketch, "E26.26.2", {"start": v(-38.86, -83.93) * mm, "end": v(-42.31, -91.7) * mm});
            skLineSegment(sketch, "E26.26.3", {"start": v(-41.14, -87.57) * mm, "end": v(-38, -88.96) * mm, "construction": true});
            skLineSegment(sketch, "E26.26.4", {"start": v(-36.37, -85.04) * mm, "end": v(-37.62, -84.48) * mm});
            skLineSegment(sketch, "E26.26.5", {"start": v(-36.37, -85.04) * mm, "end": v(-39.83, -92.8) * mm});
            skLineSegment(sketch, "E26.26.6", {"start": v(-39.83, -92.8) * mm, "end": v(-41.07, -92.25) * mm});
            skLineSegment(sketch, "E26.26.7", {"start": v(-37.62, -84.48) * mm, "end": v(-41.07, -92.25) * mm, "construction": true});
            skLineSegment(sketch, "E26.27.0", {"start": v(-29.87, -87.53) * mm, "end": v(-28.58, -87.95) * mm});
            skLineSegment(sketch, "E26.27.1", {"start": v(-32.5, -95.62) * mm, "end": v(-31.2, -96.04) * mm});
            skLineSegment(sketch, "E26.27.2", {"start": v(-29.87, -87.53) * mm, "end": v(-32.5, -95.62) * mm});
            skLineSegment(sketch, "E26.27.3", {"start": v(-31.76, -91.39) * mm, "end": v(-28.5, -92.45) * mm, "construction": true});
            skLineSegment(sketch, "E26.27.4", {"start": v(-27.29, -88.37) * mm, "end": v(-28.58, -87.95) * mm});
            skLineSegment(sketch, "E26.27.5", {"start": v(-27.29, -88.37) * mm, "end": v(-29.91, -96.46) * mm});
            skLineSegment(sketch, "E26.27.6", {"start": v(-29.91, -96.46) * mm, "end": v(-31.2, -96.04) * mm});
            skLineSegment(sketch, "E26.27.7", {"start": v(-28.58, -87.95) * mm, "end": v(-31.2, -96.04) * mm, "construction": true});
            skLineSegment(sketch, "E26.28.0", {"start": v(-20.56, -90.18) * mm, "end": v(-19.23, -90.46) * mm});
            skLineSegment(sketch, "E26.28.1", {"start": v(-22.32, -98.5) * mm, "end": v(-21, -98.77) * mm});
            skLineSegment(sketch, "E26.28.2", {"start": v(-20.56, -90.18) * mm, "end": v(-22.32, -98.5) * mm});
            skLineSegment(sketch, "E26.28.3", {"start": v(-22.03, -94.2) * mm, "end": v(-18.68, -94.92) * mm, "construction": true});
            skLineSegment(sketch, "E26.28.4", {"start": v(-17.9, -90.74) * mm, "end": v(-19.23, -90.46) * mm});
            skLineSegment(sketch, "E26.28.5", {"start": v(-17.9, -90.74) * mm, "end": v(-19.67, -99.06) * mm});
            skLineSegment(sketch, "E26.28.6", {"start": v(-19.67, -99.06) * mm, "end": v(-21, -98.77) * mm});
            skLineSegment(sketch, "E26.28.7", {"start": v(-19.23, -90.46) * mm, "end": v(-21, -98.77) * mm, "construction": true});
            skLineSegment(sketch, "E26.29.0", {"start": v(-11.02, -91.83) * mm, "end": v(-9.67, -91.97) * mm});
            skLineSegment(sketch, "E26.29.1", {"start": v(-11.9, -100.28) * mm, "end": v(-10.56, -100.43) * mm});
            skLineSegment(sketch, "E26.29.2", {"start": v(-11.02, -91.83) * mm, "end": v(-11.9, -100.28) * mm});
            skLineSegment(sketch, "E26.29.3", {"start": v(-12.06, -96) * mm, "end": v(-8.66, -96.35) * mm, "construction": true});
            skLineSegment(sketch, "E26.29.4", {"start": v(-8.32, -92.12) * mm, "end": v(-9.67, -91.97) * mm});
            skLineSegment(sketch, "E26.29.5", {"start": v(-8.32, -92.12) * mm, "end": v(-9.2, -100.57) * mm});
            skLineSegment(sketch, "E26.29.6", {"start": v(-9.2, -100.57) * mm, "end": v(-10.56, -100.43) * mm});
            skLineSegment(sketch, "E26.29.7", {"start": v(-9.67, -91.97) * mm, "end": v(-10.56, -100.43) * mm, "construction": true});
            skLineSegment(sketch, "E26.30.0", {"start": v(-1.36, -92.48) * mm, "end": v(0, -92.48) * mm});
            skLineSegment(sketch, "E26.30.1", {"start": v(-1.36, -100.98) * mm, "end": v(0, -100.98) * mm});
            skLineSegment(sketch, "E26.30.2", {"start": v(-1.36, -92.48) * mm, "end": v(-1.36, -100.98) * mm});
            skLineSegment(sketch, "E26.30.3", {"start": v(-1.96, -96.73) * mm, "end": v(1.46, -96.73) * mm, "construction": true});
            skLineSegment(sketch, "E26.30.4", {"start": v(1.36, -92.48) * mm, "end": v(0, -92.48) * mm});
            skLineSegment(sketch, "E26.30.5", {"start": v(1.36, -92.48) * mm, "end": v(1.36, -100.98) * mm});
            skLineSegment(sketch, "E26.30.6", {"start": v(1.36, -100.98) * mm, "end": v(0, -100.98) * mm});
            skLineSegment(sketch, "E26.30.7", {"start": v(0, -92.48) * mm, "end": v(0, -100.98) * mm, "construction": true});
            skLineSegment(sketch, "E26.31.0", {"start": v(8.32, -92.12) * mm, "end": v(9.67, -91.97) * mm});
            skLineSegment(sketch, "E26.31.1", {"start": v(9.2, -100.57) * mm, "end": v(10.56, -100.43) * mm});
            skLineSegment(sketch, "E26.31.2", {"start": v(8.32, -92.12) * mm, "end": v(9.2, -100.57) * mm});
            skLineSegment(sketch, "E26.31.3", {"start": v(8.16, -96.4) * mm, "end": v(11.56, -96.05) * mm, "construction": true});
            skLineSegment(sketch, "E26.31.4", {"start": v(11.02, -91.83) * mm, "end": v(9.67, -91.97) * mm});
            skLineSegment(sketch, "E26.31.5", {"start": v(11.02, -91.83) * mm, "end": v(11.9, -100.28) * mm});
            skLineSegment(sketch, "E26.31.6", {"start": v(11.9, -100.28) * mm, "end": v(10.56, -100.43) * mm});
            skLineSegment(sketch, "E26.31.7", {"start": v(9.67, -91.97) * mm, "end": v(10.56, -100.43) * mm, "construction": true});
            skLineSegment(sketch, "E26.32.0", {"start": v(17.9, -90.74) * mm, "end": v(19.23, -90.46) * mm});
            skLineSegment(sketch, "E26.32.1", {"start": v(19.67, -99.06) * mm, "end": v(21, -98.77) * mm});
            skLineSegment(sketch, "E26.32.2", {"start": v(17.9, -90.74) * mm, "end": v(19.67, -99.06) * mm});
            skLineSegment(sketch, "E26.32.3", {"start": v(18.2, -95.02) * mm, "end": v(21.54, -94.31) * mm, "construction": true});
            skLineSegment(sketch, "E26.32.4", {"start": v(20.56, -90.18) * mm, "end": v(19.23, -90.46) * mm});
            skLineSegment(sketch, "E26.32.5", {"start": v(20.56, -90.18) * mm, "end": v(22.32, -98.5) * mm});
            skLineSegment(sketch, "E26.32.6", {"start": v(22.32, -98.5) * mm, "end": v(21, -98.77) * mm});
            skLineSegment(sketch, "E26.32.7", {"start": v(19.23, -90.46) * mm, "end": v(21, -98.77) * mm, "construction": true});
            skLineSegment(sketch, "E26.33.0", {"start": v(27.29, -88.37) * mm, "end": v(28.58, -87.95) * mm});
            skLineSegment(sketch, "E26.33.1", {"start": v(29.91, -96.46) * mm, "end": v(31.2, -96.04) * mm});
            skLineSegment(sketch, "E26.33.2", {"start": v(27.29, -88.37) * mm, "end": v(29.91, -96.46) * mm});
            skLineSegment(sketch, "E26.33.3", {"start": v(28.02, -92.6) * mm, "end": v(31.28, -91.54) * mm, "construction": true});
            skLineSegment(sketch, "E26.33.4", {"start": v(29.87, -87.53) * mm, "end": v(28.58, -87.95) * mm});
            skLineSegment(sketch, "E26.33.5", {"start": v(29.87, -87.53) * mm, "end": v(32.5, -95.62) * mm});
            skLineSegment(sketch, "E26.33.6", {"start": v(32.5, -95.62) * mm, "end": v(31.2, -96.04) * mm});
            skLineSegment(sketch, "E26.33.7", {"start": v(28.58, -87.95) * mm, "end": v(31.2, -96.04) * mm, "construction": true});
            skLineSegment(sketch, "E26.34.0", {"start": v(36.37, -85.04) * mm, "end": v(37.62, -84.48) * mm});
            skLineSegment(sketch, "E26.34.1", {"start": v(39.83, -92.8) * mm, "end": v(41.07, -92.25) * mm});
            skLineSegment(sketch, "E26.34.2", {"start": v(36.37, -85.04) * mm, "end": v(39.83, -92.8) * mm});
            skLineSegment(sketch, "E26.34.3", {"start": v(37.55, -89.17) * mm, "end": v(40.68, -87.77) * mm, "construction": true});
            skLineSegment(sketch, "E26.34.4", {"start": v(38.86, -83.93) * mm, "end": v(37.62, -84.48) * mm});
            skLineSegment(sketch, "E26.34.5", {"start": v(38.86, -83.93) * mm, "end": v(42.31, -91.7) * mm});
            skLineSegment(sketch, "E26.34.6", {"start": v(42.31, -91.7) * mm, "end": v(41.07, -92.25) * mm});
            skLineSegment(sketch, "E26.34.7", {"start": v(37.62, -84.48) * mm, "end": v(41.07, -92.25) * mm, "construction": true});
            skLineSegment(sketch, "E26.35.0", {"start": v(45.06, -80.77) * mm, "end": v(46.24, -80.1) * mm});
            skLineSegment(sketch, "E26.35.1", {"start": v(49.31, -88.13) * mm, "end": v(50.49, -87.45) * mm});
            skLineSegment(sketch, "E26.35.2", {"start": v(45.06, -80.77) * mm, "end": v(49.31, -88.13) * mm});
            skLineSegment(sketch, "E26.35.3", {"start": v(46.67, -84.75) * mm, "end": v(49.63, -83.04) * mm, "construction": true});
            skLineSegment(sketch, "E26.35.4", {"start": v(47.42, -79.41) * mm, "end": v(46.24, -80.1) * mm});
            skLineSegment(sketch, "E26.35.5", {"start": v(47.42, -79.41) * mm, "end": v(51.67, -86.77) * mm});
            skLineSegment(sketch, "E26.35.6", {"start": v(51.67, -86.77) * mm, "end": v(50.49, -87.45) * mm});
            skLineSegment(sketch, "E26.35.7", {"start": v(46.24, -80.1) * mm, "end": v(50.49, -87.45) * mm, "construction": true});
            skLineSegment(sketch, "E26.36.0", {"start": v(53.26, -75.62) * mm, "end": v(54.36, -74.82) * mm});
            skLineSegment(sketch, "E26.36.1", {"start": v(58.26, -82.5) * mm, "end": v(59.35, -81.7) * mm});
            skLineSegment(sketch, "E26.36.2", {"start": v(53.26, -75.62) * mm, "end": v(58.26, -82.5) * mm});
            skLineSegment(sketch, "E26.36.3", {"start": v(55.27, -79.4) * mm, "end": v(58.04, -77.4) * mm, "construction": true});
            skLineSegment(sketch, "E26.36.4", {"start": v(55.46, -74.02) * mm, "end": v(54.36, -74.82) * mm});
            skLineSegment(sketch, "E26.36.5", {"start": v(55.46, -74.02) * mm, "end": v(60.45, -80.9) * mm});
            skLineSegment(sketch, "E26.36.6", {"start": v(60.45, -80.9) * mm, "end": v(59.35, -81.7) * mm});
            skLineSegment(sketch, "E26.36.7", {"start": v(54.36, -74.82) * mm, "end": v(59.35, -81.7) * mm, "construction": true});
            skLineSegment(sketch, "E26.37.0", {"start": v(60.87, -69.63) * mm, "end": v(61.88, -68.73) * mm});
            skLineSegment(sketch, "E26.37.1", {"start": v(66.56, -75.95) * mm, "end": v(67.57, -75.04) * mm});
            skLineSegment(sketch, "E26.37.2", {"start": v(60.87, -69.63) * mm, "end": v(66.56, -75.95) * mm});
            skLineSegment(sketch, "E26.37.3", {"start": v(63.27, -73.2) * mm, "end": v(65.8, -70.9) * mm, "construction": true});
            skLineSegment(sketch, "E26.37.4", {"start": v(62.9, -67.82) * mm, "end": v(61.88, -68.73) * mm});
            skLineSegment(sketch, "E26.37.5", {"start": v(62.9, -67.82) * mm, "end": v(68.58, -74.13) * mm});
            skLineSegment(sketch, "E26.37.6", {"start": v(68.58, -74.13) * mm, "end": v(67.57, -75.04) * mm});
            skLineSegment(sketch, "E26.37.7", {"start": v(61.88, -68.73) * mm, "end": v(67.57, -75.04) * mm, "construction": true});
            skLineSegment(sketch, "E26.38.0", {"start": v(67.82, -62.9) * mm, "end": v(68.73, -61.88) * mm});
            skLineSegment(sketch, "E26.38.1", {"start": v(74.13, -68.58) * mm, "end": v(75.04, -67.57) * mm});
            skLineSegment(sketch, "E26.38.2", {"start": v(67.82, -62.9) * mm, "end": v(74.13, -68.58) * mm});
            skLineSegment(sketch, "E26.38.3", {"start": v(70.57, -66.18) * mm, "end": v(72.86, -63.64) * mm, "construction": true});
            skLineSegment(sketch, "E26.38.4", {"start": v(69.63, -60.87) * mm, "end": v(68.73, -61.88) * mm});
            skLineSegment(sketch, "E26.38.5", {"start": v(69.63, -60.87) * mm, "end": v(75.95, -66.56) * mm});
            skLineSegment(sketch, "E26.38.6", {"start": v(75.95, -66.56) * mm, "end": v(75.04, -67.57) * mm});
            skLineSegment(sketch, "E26.38.7", {"start": v(68.73, -61.88) * mm, "end": v(75.04, -67.57) * mm, "construction": true});
            skLineSegment(sketch, "E26.39.0", {"start": v(74.02, -55.46) * mm, "end": v(74.82, -54.36) * mm});
            skLineSegment(sketch, "E26.39.1", {"start": v(80.9, -60.45) * mm, "end": v(81.7, -59.35) * mm});
            skLineSegment(sketch, "E26.39.2", {"start": v(74.02, -55.46) * mm, "end": v(80.9, -60.45) * mm});
            skLineSegment(sketch, "E26.39.3", {"start": v(77.1, -58.44) * mm, "end": v(79.11, -55.68) * mm, "construction": true});
            skLineSegment(sketch, "E26.39.4", {"start": v(75.62, -53.26) * mm, "end": v(74.82, -54.36) * mm});
            skLineSegment(sketch, "E26.39.5", {"start": v(75.62, -53.26) * mm, "end": v(82.5, -58.26) * mm});
            skLineSegment(sketch, "E26.39.6", {"start": v(82.5, -58.26) * mm, "end": v(81.7, -59.35) * mm});
            skLineSegment(sketch, "E26.39.7", {"start": v(74.82, -54.36) * mm, "end": v(81.7, -59.35) * mm, "construction": true});
            skLineSegment(sketch, "E26.40.0", {"start": v(79.41, -47.42) * mm, "end": v(80.1, -46.24) * mm});
            skLineSegment(sketch, "E26.40.1", {"start": v(86.77, -51.67) * mm, "end": v(87.45, -50.5) * mm});
            skLineSegment(sketch, "E26.40.2", {"start": v(79.41, -47.42) * mm, "end": v(86.77, -51.67) * mm});
            skLineSegment(sketch, "E26.40.3", {"start": v(82.79, -50.06) * mm, "end": v(84.5, -47.1) * mm, "construction": true});
            skLineSegment(sketch, "E26.40.4", {"start": v(80.77, -45.06) * mm, "end": v(80.1, -46.24) * mm});
            skLineSegment(sketch, "E26.40.5", {"start": v(80.77, -45.06) * mm, "end": v(88.13, -49.31) * mm});
            skLineSegment(sketch, "E26.40.6", {"start": v(88.13, -49.31) * mm, "end": v(87.45, -50.5) * mm});
            skLineSegment(sketch, "E26.40.7", {"start": v(80.1, -46.24) * mm, "end": v(87.45, -50.5) * mm, "construction": true});
            skLineSegment(sketch, "E26.41.0", {"start": v(83.93, -38.86) * mm, "end": v(84.48, -37.62) * mm});
            skLineSegment(sketch, "E26.41.1", {"start": v(91.7, -42.31) * mm, "end": v(92.25, -41.07) * mm});
            skLineSegment(sketch, "E26.41.2", {"start": v(83.93, -38.86) * mm, "end": v(91.7, -42.31) * mm});
            skLineSegment(sketch, "E26.41.3", {"start": v(87.57, -41.14) * mm, "end": v(88.96, -38) * mm, "construction": true});
            skLineSegment(sketch, "E26.41.4", {"start": v(85.04, -36.37) * mm, "end": v(84.48, -37.62) * mm});
            skLineSegment(sketch, "E26.41.5", {"start": v(85.04, -36.37) * mm, "end": v(92.8, -39.83) * mm});
            skLineSegment(sketch, "E26.41.6", {"start": v(92.8, -39.83) * mm, "end": v(92.25, -41.07) * mm});
            skLineSegment(sketch, "E26.41.7", {"start": v(84.48, -37.62) * mm, "end": v(92.25, -41.07) * mm, "construction": true});
            skLineSegment(sketch, "E26.42.0", {"start": v(87.53, -29.87) * mm, "end": v(87.95, -28.58) * mm});
            skLineSegment(sketch, "E26.42.1", {"start": v(95.62, -32.5) * mm, "end": v(96.04, -31.2) * mm});
            skLineSegment(sketch, "E26.42.2", {"start": v(87.53, -29.87) * mm, "end": v(95.62, -32.5) * mm});
            skLineSegment(sketch, "E26.42.3", {"start": v(91.39, -31.76) * mm, "end": v(92.45, -28.5) * mm, "construction": true});
            skLineSegment(sketch, "E26.42.4", {"start": v(88.37, -27.29) * mm, "end": v(87.95, -28.58) * mm});
            skLineSegment(sketch, "E26.42.5", {"start": v(88.37, -27.29) * mm, "end": v(96.46, -29.91) * mm});
            skLineSegment(sketch, "E26.42.6", {"start": v(96.46, -29.91) * mm, "end": v(96.04, -31.2) * mm});
            skLineSegment(sketch, "E26.42.7", {"start": v(87.95, -28.58) * mm, "end": v(96.04, -31.2) * mm, "construction": true});
            skLineSegment(sketch, "E26.43.0", {"start": v(90.18, -20.56) * mm, "end": v(90.46, -19.23) * mm});
            skLineSegment(sketch, "E26.43.1", {"start": v(98.5, -22.32) * mm, "end": v(98.77, -21) * mm});
            skLineSegment(sketch, "E26.43.2", {"start": v(90.18, -20.56) * mm, "end": v(98.5, -22.32) * mm});
            skLineSegment(sketch, "E26.43.3", {"start": v(94.2, -22.03) * mm, "end": v(94.92, -18.68) * mm, "construction": true});
            skLineSegment(sketch, "E26.43.4", {"start": v(90.74, -17.9) * mm, "end": v(90.46, -19.23) * mm});
            skLineSegment(sketch, "E26.43.5", {"start": v(90.74, -17.9) * mm, "end": v(99.06, -19.67) * mm});
            skLineSegment(sketch, "E26.43.6", {"start": v(99.06, -19.67) * mm, "end": v(98.77, -21) * mm});
            skLineSegment(sketch, "E26.43.7", {"start": v(90.46, -19.23) * mm, "end": v(98.77, -21) * mm, "construction": true});
            skLineSegment(sketch, "E26.44.0", {"start": v(91.83, -11.02) * mm, "end": v(91.97, -9.67) * mm});
            skLineSegment(sketch, "E26.44.1", {"start": v(100.28, -11.9) * mm, "end": v(100.43, -10.56) * mm});
            skLineSegment(sketch, "E26.44.2", {"start": v(91.83, -11.02) * mm, "end": v(100.28, -11.9) * mm});
            skLineSegment(sketch, "E26.44.3", {"start": v(96, -12.06) * mm, "end": v(96.35, -8.66) * mm, "construction": true});
            skLineSegment(sketch, "E26.44.4", {"start": v(92.12, -8.32) * mm, "end": v(91.97, -9.67) * mm});
            skLineSegment(sketch, "E26.44.5", {"start": v(92.12, -8.32) * mm, "end": v(100.57, -9.2) * mm});
            skLineSegment(sketch, "E26.44.6", {"start": v(100.57, -9.2) * mm, "end": v(100.43, -10.56) * mm});
            skLineSegment(sketch, "E26.44.7", {"start": v(91.97, -9.67) * mm, "end": v(100.43, -10.56) * mm, "construction": true});
            skLineSegment(sketch, "E26.45.0", {"start": v(92.48, -1.36) * mm, "end": v(92.48, 0) * mm});
            skLineSegment(sketch, "E26.45.1", {"start": v(100.98, -1.36) * mm, "end": v(100.98, 0) * mm});
            skLineSegment(sketch, "E26.45.2", {"start": v(92.48, -1.36) * mm, "end": v(100.98, -1.36) * mm});
            skLineSegment(sketch, "E26.45.3", {"start": v(96.73, -1.96) * mm, "end": v(96.73, 1.46) * mm, "construction": true});
            skLineSegment(sketch, "E26.45.4", {"start": v(92.48, 1.36) * mm, "end": v(92.48, 0) * mm});
            skLineSegment(sketch, "E26.45.5", {"start": v(92.48, 1.36) * mm, "end": v(100.98, 1.36) * mm});
            skLineSegment(sketch, "E26.45.6", {"start": v(100.98, 1.36) * mm, "end": v(100.98, 0) * mm});
            skLineSegment(sketch, "E26.45.7", {"start": v(92.48, 0) * mm, "end": v(100.98, 0) * mm, "construction": true});
            skLineSegment(sketch, "E26.46.0", {"start": v(92.12, 8.32) * mm, "end": v(91.97, 9.67) * mm});
            skLineSegment(sketch, "E26.46.1", {"start": v(100.57, 9.2) * mm, "end": v(100.43, 10.56) * mm});
            skLineSegment(sketch, "E26.46.2", {"start": v(92.12, 8.32) * mm, "end": v(100.57, 9.2) * mm});
            skLineSegment(sketch, "E26.46.3", {"start": v(96.4, 8.16) * mm, "end": v(96.05, 11.56) * mm, "construction": true});
            skLineSegment(sketch, "E26.46.4", {"start": v(91.83, 11.02) * mm, "end": v(91.97, 9.67) * mm});
            skLineSegment(sketch, "E26.46.5", {"start": v(91.83, 11.02) * mm, "end": v(100.28, 11.9) * mm});
            skLineSegment(sketch, "E26.46.6", {"start": v(100.28, 11.9) * mm, "end": v(100.43, 10.56) * mm});
            skLineSegment(sketch, "E26.46.7", {"start": v(91.97, 9.67) * mm, "end": v(100.43, 10.56) * mm, "construction": true});
            skLineSegment(sketch, "E26.47.0", {"start": v(90.74, 17.9) * mm, "end": v(90.46, 19.23) * mm});
            skLineSegment(sketch, "E26.47.1", {"start": v(99.06, 19.67) * mm, "end": v(98.77, 21) * mm});
            skLineSegment(sketch, "E26.47.2", {"start": v(90.74, 17.9) * mm, "end": v(99.06, 19.67) * mm});
            skLineSegment(sketch, "E26.47.3", {"start": v(95.02, 18.2) * mm, "end": v(94.31, 21.54) * mm, "construction": true});
            skLineSegment(sketch, "E26.47.4", {"start": v(90.18, 20.56) * mm, "end": v(90.46, 19.23) * mm});
            skLineSegment(sketch, "E26.47.5", {"start": v(90.18, 20.56) * mm, "end": v(98.5, 22.32) * mm});
            skLineSegment(sketch, "E26.47.6", {"start": v(98.5, 22.32) * mm, "end": v(98.77, 21) * mm});
            skLineSegment(sketch, "E26.47.7", {"start": v(90.46, 19.23) * mm, "end": v(98.77, 21) * mm, "construction": true});
            skLineSegment(sketch, "E26.48.0", {"start": v(88.37, 27.29) * mm, "end": v(87.95, 28.58) * mm});
            skLineSegment(sketch, "E26.48.1", {"start": v(96.46, 29.91) * mm, "end": v(96.04, 31.2) * mm});
            skLineSegment(sketch, "E26.48.2", {"start": v(88.37, 27.29) * mm, "end": v(96.46, 29.91) * mm});
            skLineSegment(sketch, "E26.48.3", {"start": v(92.6, 28.02) * mm, "end": v(91.54, 31.28) * mm, "construction": true});
            skLineSegment(sketch, "E26.48.4", {"start": v(87.53, 29.87) * mm, "end": v(87.95, 28.58) * mm});
            skLineSegment(sketch, "E26.48.5", {"start": v(87.53, 29.87) * mm, "end": v(95.62, 32.5) * mm});
            skLineSegment(sketch, "E26.48.6", {"start": v(95.62, 32.5) * mm, "end": v(96.04, 31.2) * mm});
            skLineSegment(sketch, "E26.48.7", {"start": v(87.95, 28.58) * mm, "end": v(96.04, 31.2) * mm, "construction": true});
            skLineSegment(sketch, "E26.49.0", {"start": v(85.04, 36.37) * mm, "end": v(84.48, 37.62) * mm});
            skLineSegment(sketch, "E26.49.1", {"start": v(92.8, 39.83) * mm, "end": v(92.25, 41.07) * mm});
            skLineSegment(sketch, "E26.49.2", {"start": v(85.04, 36.37) * mm, "end": v(92.8, 39.83) * mm});
            skLineSegment(sketch, "E26.49.3", {"start": v(89.17, 37.55) * mm, "end": v(87.77, 40.68) * mm, "construction": true});
            skLineSegment(sketch, "E26.49.4", {"start": v(83.93, 38.86) * mm, "end": v(84.48, 37.62) * mm});
            skLineSegment(sketch, "E26.49.5", {"start": v(83.93, 38.86) * mm, "end": v(91.7, 42.31) * mm});
            skLineSegment(sketch, "E26.49.6", {"start": v(91.7, 42.31) * mm, "end": v(92.25, 41.07) * mm});
            skLineSegment(sketch, "E26.49.7", {"start": v(84.48, 37.62) * mm, "end": v(92.25, 41.07) * mm, "construction": true});
            skLineSegment(sketch, "E26.50.0", {"start": v(80.77, 45.06) * mm, "end": v(80.1, 46.24) * mm});
            skLineSegment(sketch, "E26.50.1", {"start": v(88.13, 49.31) * mm, "end": v(87.45, 50.49) * mm});
            skLineSegment(sketch, "E26.50.2", {"start": v(80.77, 45.06) * mm, "end": v(88.13, 49.31) * mm});
            skLineSegment(sketch, "E26.50.3", {"start": v(84.75, 46.67) * mm, "end": v(83.04, 49.63) * mm, "construction": true});
            skLineSegment(sketch, "E26.50.4", {"start": v(79.41, 47.42) * mm, "end": v(80.1, 46.24) * mm});
            skLineSegment(sketch, "E26.50.5", {"start": v(79.41, 47.42) * mm, "end": v(86.77, 51.67) * mm});
            skLineSegment(sketch, "E26.50.6", {"start": v(86.77, 51.67) * mm, "end": v(87.45, 50.49) * mm});
            skLineSegment(sketch, "E26.50.7", {"start": v(80.1, 46.24) * mm, "end": v(87.45, 50.49) * mm, "construction": true});
            skLineSegment(sketch, "E26.51.0", {"start": v(75.62, 53.26) * mm, "end": v(74.82, 54.36) * mm});
            skLineSegment(sketch, "E26.51.1", {"start": v(82.5, 58.26) * mm, "end": v(81.7, 59.35) * mm});
            skLineSegment(sketch, "E26.51.2", {"start": v(75.62, 53.26) * mm, "end": v(82.5, 58.26) * mm});
            skLineSegment(sketch, "E26.51.3", {"start": v(79.4, 55.27) * mm, "end": v(77.4, 58.04) * mm, "construction": true});
            skLineSegment(sketch, "E26.51.4", {"start": v(74.02, 55.46) * mm, "end": v(74.82, 54.36) * mm});
            skLineSegment(sketch, "E26.51.5", {"start": v(74.02, 55.46) * mm, "end": v(80.9, 60.45) * mm});
            skLineSegment(sketch, "E26.51.6", {"start": v(80.9, 60.45) * mm, "end": v(81.7, 59.35) * mm});
            skLineSegment(sketch, "E26.51.7", {"start": v(74.82, 54.36) * mm, "end": v(81.7, 59.35) * mm, "construction": true});
            skLineSegment(sketch, "E26.52.0", {"start": v(69.63, 60.87) * mm, "end": v(68.73, 61.88) * mm});
            skLineSegment(sketch, "E26.52.1", {"start": v(75.95, 66.56) * mm, "end": v(75.04, 67.57) * mm});
            skLineSegment(sketch, "E26.52.2", {"start": v(69.63, 60.87) * mm, "end": v(75.95, 66.56) * mm});
            skLineSegment(sketch, "E26.52.3", {"start": v(73.2, 63.27) * mm, "end": v(70.9, 65.8) * mm, "construction": true});
            skLineSegment(sketch, "E26.52.4", {"start": v(67.82, 62.9) * mm, "end": v(68.73, 61.88) * mm});
            skLineSegment(sketch, "E26.52.5", {"start": v(67.82, 62.9) * mm, "end": v(74.13, 68.58) * mm});
            skLineSegment(sketch, "E26.52.6", {"start": v(74.13, 68.58) * mm, "end": v(75.04, 67.57) * mm});
            skLineSegment(sketch, "E26.52.7", {"start": v(68.73, 61.88) * mm, "end": v(75.04, 67.57) * mm, "construction": true});
            skLineSegment(sketch, "E26.53.0", {"start": v(62.9, 67.82) * mm, "end": v(61.88, 68.73) * mm});
            skLineSegment(sketch, "E26.53.1", {"start": v(68.58, 74.13) * mm, "end": v(67.57, 75.04) * mm});
            skLineSegment(sketch, "E26.53.2", {"start": v(62.9, 67.82) * mm, "end": v(68.58, 74.13) * mm});
            skLineSegment(sketch, "E26.53.3", {"start": v(66.18, 70.57) * mm, "end": v(63.64, 72.86) * mm, "construction": true});
            skLineSegment(sketch, "E26.53.4", {"start": v(60.87, 69.63) * mm, "end": v(61.88, 68.73) * mm});
            skLineSegment(sketch, "E26.53.5", {"start": v(60.87, 69.63) * mm, "end": v(66.56, 75.95) * mm});
            skLineSegment(sketch, "E26.53.6", {"start": v(66.56, 75.95) * mm, "end": v(67.57, 75.04) * mm});
            skLineSegment(sketch, "E26.53.7", {"start": v(61.88, 68.73) * mm, "end": v(67.57, 75.04) * mm, "construction": true});
            skLineSegment(sketch, "E26.54.0", {"start": v(55.46, 74.02) * mm, "end": v(54.36, 74.82) * mm});
            skLineSegment(sketch, "E26.54.1", {"start": v(60.45, 80.9) * mm, "end": v(59.35, 81.7) * mm});
            skLineSegment(sketch, "E26.54.2", {"start": v(55.46, 74.02) * mm, "end": v(60.45, 80.9) * mm});
            skLineSegment(sketch, "E26.54.3", {"start": v(58.44, 77.1) * mm, "end": v(55.68, 79.11) * mm, "construction": true});
            skLineSegment(sketch, "E26.54.4", {"start": v(53.26, 75.62) * mm, "end": v(54.36, 74.82) * mm});
            skLineSegment(sketch, "E26.54.5", {"start": v(53.26, 75.62) * mm, "end": v(58.26, 82.5) * mm});
            skLineSegment(sketch, "E26.54.6", {"start": v(58.26, 82.5) * mm, "end": v(59.35, 81.7) * mm});
            skLineSegment(sketch, "E26.54.7", {"start": v(54.36, 74.82) * mm, "end": v(59.35, 81.7) * mm, "construction": true});
            skLineSegment(sketch, "E26.55.0", {"start": v(47.42, 79.41) * mm, "end": v(46.24, 80.1) * mm});
            skLineSegment(sketch, "E26.55.1", {"start": v(51.67, 86.77) * mm, "end": v(50.49, 87.45) * mm});
            skLineSegment(sketch, "E26.55.2", {"start": v(47.42, 79.41) * mm, "end": v(51.67, 86.77) * mm});
            skLineSegment(sketch, "E26.55.3", {"start": v(50.06, 82.79) * mm, "end": v(47.1, 84.5) * mm, "construction": true});
            skLineSegment(sketch, "E26.55.4", {"start": v(45.06, 80.77) * mm, "end": v(46.24, 80.1) * mm});
            skLineSegment(sketch, "E26.55.5", {"start": v(45.06, 80.77) * mm, "end": v(49.31, 88.13) * mm});
            skLineSegment(sketch, "E26.55.6", {"start": v(49.31, 88.13) * mm, "end": v(50.49, 87.45) * mm});
            skLineSegment(sketch, "E26.55.7", {"start": v(46.24, 80.1) * mm, "end": v(50.49, 87.45) * mm, "construction": true});
            skLineSegment(sketch, "E26.56.0", {"start": v(38.86, 83.93) * mm, "end": v(37.62, 84.48) * mm});
            skLineSegment(sketch, "E26.56.1", {"start": v(42.31, 91.7) * mm, "end": v(41.07, 92.25) * mm});
            skLineSegment(sketch, "E26.56.2", {"start": v(38.86, 83.93) * mm, "end": v(42.31, 91.7) * mm});
            skLineSegment(sketch, "E26.56.3", {"start": v(41.14, 87.57) * mm, "end": v(38, 88.96) * mm, "construction": true});
            skLineSegment(sketch, "E26.56.4", {"start": v(36.37, 85.04) * mm, "end": v(37.62, 84.48) * mm});
            skLineSegment(sketch, "E26.56.5", {"start": v(36.37, 85.04) * mm, "end": v(39.83, 92.8) * mm});
            skLineSegment(sketch, "E26.56.6", {"start": v(39.83, 92.8) * mm, "end": v(41.07, 92.25) * mm});
            skLineSegment(sketch, "E26.56.7", {"start": v(37.62, 84.48) * mm, "end": v(41.07, 92.25) * mm, "construction": true});
            skLineSegment(sketch, "E26.57.0", {"start": v(29.87, 87.53) * mm, "end": v(28.58, 87.95) * mm});
            skLineSegment(sketch, "E26.57.1", {"start": v(32.5, 95.62) * mm, "end": v(31.2, 96.04) * mm});
            skLineSegment(sketch, "E26.57.2", {"start": v(29.87, 87.53) * mm, "end": v(32.5, 95.62) * mm});
            skLineSegment(sketch, "E26.57.3", {"start": v(31.76, 91.39) * mm, "end": v(28.5, 92.45) * mm, "construction": true});
            skLineSegment(sketch, "E26.57.4", {"start": v(27.29, 88.37) * mm, "end": v(28.58, 87.95) * mm});
            skLineSegment(sketch, "E26.57.5", {"start": v(27.29, 88.37) * mm, "end": v(29.91, 96.46) * mm});
            skLineSegment(sketch, "E26.57.6", {"start": v(29.91, 96.46) * mm, "end": v(31.2, 96.04) * mm});
            skLineSegment(sketch, "E26.57.7", {"start": v(28.58, 87.95) * mm, "end": v(31.2, 96.04) * mm, "construction": true});
            skLineSegment(sketch, "E26.58.0", {"start": v(20.56, 90.18) * mm, "end": v(19.23, 90.46) * mm});
            skLineSegment(sketch, "E26.58.1", {"start": v(22.32, 98.5) * mm, "end": v(21, 98.77) * mm});
            skLineSegment(sketch, "E26.58.2", {"start": v(20.56, 90.18) * mm, "end": v(22.32, 98.5) * mm});
            skLineSegment(sketch, "E26.58.3", {"start": v(22.03, 94.2) * mm, "end": v(18.68, 94.92) * mm, "construction": true});
            skLineSegment(sketch, "E26.58.4", {"start": v(17.9, 90.74) * mm, "end": v(19.23, 90.46) * mm});
            skLineSegment(sketch, "E26.58.5", {"start": v(17.9, 90.74) * mm, "end": v(19.67, 99.06) * mm});
            skLineSegment(sketch, "E26.58.6", {"start": v(19.67, 99.06) * mm, "end": v(21, 98.77) * mm});
            skLineSegment(sketch, "E26.58.7", {"start": v(19.23, 90.46) * mm, "end": v(21, 98.77) * mm, "construction": true});
            skLineSegment(sketch, "E26.59.0", {"start": v(11.02, 91.83) * mm, "end": v(9.67, 91.97) * mm});
            skLineSegment(sketch, "E26.59.1", {"start": v(11.9, 100.28) * mm, "end": v(10.56, 100.43) * mm});
            skLineSegment(sketch, "E26.59.2", {"start": v(11.02, 91.83) * mm, "end": v(11.9, 100.28) * mm});
            skLineSegment(sketch, "E26.59.3", {"start": v(12.06, 96) * mm, "end": v(8.66, 96.35) * mm, "construction": true});
            skLineSegment(sketch, "E26.59.4", {"start": v(8.32, 92.12) * mm, "end": v(9.67, 91.97) * mm});
            skLineSegment(sketch, "E26.59.5", {"start": v(8.32, 92.12) * mm, "end": v(9.2, 100.57) * mm});
            skLineSegment(sketch, "E26.59.6", {"start": v(9.2, 100.57) * mm, "end": v(10.56, 100.43) * mm});
            skLineSegment(sketch, "E26.59.7", {"start": v(9.67, 91.97) * mm, "end": v(10.56, 100.43) * mm, "construction": true});
            skPoint(sketch, "E26.center", {"position": v(0, 0) * mm});
            skSolve(sketch);
        }
        {
            var Q0;
            Q0 = qSketchRegion(id + "F13", true);
            extrude(context, id + "F14", {"entities" : qUnion([Q0]), "operationType" : NewBodyOperationType.REMOVE, "depth" : 25 * mm, "offsetDistance" : 25 * mm, "hasSecondDirection" : true, "secondDirectionOppositeDirection" : false, "secondDirectionDepth" : 2 * mm});
        }
        {
            var Q0;
            Q0=makeQuery(id+"F1.opRevolve","SWEPT_FACE",FACE,{"disambiguationData":[OSD([sQuery(id+"F0.wireOp",EDGE,"E5")])]});
            var sketch = newSketch(context, id + "F15", { "sketchPlane" : qUnion([Q0])});
            skLineSegment(sketch, "E27", {"start": v(0, 0) * mm, "end": v(25.68, 95.85) * mm, "construction": true});
            skLineSegment(sketch, "E28", {"start": v(0, 0) * mm, "end": v(70.17, 70.17) * mm, "construction": true});
            skLineSegment(sketch, "E29", {"start": v(0, 0) * mm, "end": v(95.85, 25.68) * mm, "construction": true});
            skLineSegment(sketch, "E30", {"start": v(0, 0) * mm, "end": v(95.85, -25.68) * mm, "construction": true});
            skLineSegment(sketch, "E31", {"start": v(0, 0) * mm, "end": v(70.17, -70.17) * mm, "construction": true});
            skLineSegment(sketch, "E32", {"start": v(0, 0) * mm, "end": v(25.68, -95.85) * mm, "construction": true});
            skLineSegment(sketch, "E33", {"start": v(0, 0) * mm, "end": v(104.73, 0) * mm, "construction": true});
            skArc(sketch, "E34", {"start": v(22.25, -102.34) * mm, "mid": v(27.1, -101.16) * mm, "end": v(31.9, -99.75) * mm});
            skArc(sketch, "E35", {"start": v(21.47, -99.44) * mm, "mid": v(26.33, -98.26) * mm, "end": v(31.13, -96.85) * mm});
            skLineSegment(sketch, "E36", {"start": v(25.68, 95.85) * mm, "end": v(30.51, 94.55) * mm, "construction": true});
            skLineSegment(sketch, "E37.MirrorCS", {"start": v(25.68, 95.85) * mm, "end": v(20.85, 97.14) * mm, "construction": true});
            skLineSegment(sketch, "E38", {"start": v(21.47, 99.44) * mm, "end": v(22.25, 102.34) * mm});
            skLineSegment(sketch, "E39", {"start": v(31.13, 96.85) * mm, "end": v(31.9, 99.75) * mm});
            skLineSegment(sketch, "E40", {"start": v(70.17, 70.17) * mm, "end": v(73.7, 66.63) * mm, "construction": true});
            skLineSegment(sketch, "E41.MirrorCS", {"start": v(70.17, 70.17) * mm, "end": v(66.63, 73.7) * mm, "construction": true});
            skLineSegment(sketch, "E42", {"start": v(75.38, 68.31) * mm, "end": v(77.5, 70.44) * mm});
            skLineSegment(sketch, "E43", {"start": v(68.31, 75.38) * mm, "end": v(70.44, 77.5) * mm});
            skArc(sketch, "E44.trimOffspring", {"start": v(31.9, 99.75) * mm, "mid": v(27.1, 101.16) * mm, "end": v(22.25, 102.34) * mm});
            skArc(sketch, "E45.trimOffspring", {"start": v(31.13, 96.85) * mm, "mid": v(26.33, 98.26) * mm, "end": v(21.47, 99.44) * mm});
            skLineSegment(sketch, "E46", {"start": v(95.85, 25.68) * mm, "end": v(97.14, 20.85) * mm, "construction": true});
            skLineSegment(sketch, "E47.MirrorCS", {"start": v(95.85, 25.68) * mm, "end": v(94.55, 30.51) * mm, "construction": true});
            skLineSegment(sketch, "E48", {"start": v(96.85, 31.13) * mm, "end": v(99.75, 31.9) * mm});
            skLineSegment(sketch, "E49", {"start": v(99.44, 21.47) * mm, "end": v(102.34, 22.25) * mm});
            skArc(sketch, "E50.trimOffspring", {"start": v(75.38, 68.31) * mm, "mid": v(71.93, 71.93) * mm, "end": v(68.31, 75.38) * mm});
            skArc(sketch, "E51.trimOffspring", {"start": v(77.5, 70.44) * mm, "mid": v(74.06, 74.06) * mm, "end": v(70.44, 77.5) * mm});
            skLineSegment(sketch, "E52", {"start": v(95.85, -25.68) * mm, "end": v(94.55, -30.51) * mm, "construction": true});
            skLineSegment(sketch, "E53.MirrorCS", {"start": v(95.85, -25.68) * mm, "end": v(97.14, -20.85) * mm, "construction": true});
            skLineSegment(sketch, "E54", {"start": v(96.85, -31.13) * mm, "end": v(99.75, -31.9) * mm});
            skLineSegment(sketch, "E55", {"start": v(99.44, -21.47) * mm, "end": v(102.34, -22.25) * mm});
            skArc(sketch, "E56.trimOffspring", {"start": v(99.44, 21.47) * mm, "mid": v(98.26, 26.33) * mm, "end": v(96.85, 31.13) * mm});
            skArc(sketch, "E57.trimOffspring", {"start": v(102.34, 22.25) * mm, "mid": v(101.16, 27.1) * mm, "end": v(99.75, 31.9) * mm});
            skLineSegment(sketch, "E58", {"start": v(70.17, -70.17) * mm, "end": v(66.63, -73.7) * mm, "construction": true});
            skLineSegment(sketch, "E59.MirrorCS", {"start": v(70.17, -70.17) * mm, "end": v(73.7, -66.63) * mm, "construction": true});
            skLineSegment(sketch, "E60", {"start": v(75.38, -68.31) * mm, "end": v(77.5, -70.44) * mm});
            skLineSegment(sketch, "E61", {"start": v(68.31, -75.38) * mm, "end": v(70.44, -77.5) * mm});
            skArc(sketch, "E62.trimOffspring", {"start": v(99.75, -31.9) * mm, "mid": v(101.16, -27.1) * mm, "end": v(102.34, -22.25) * mm});
            skArc(sketch, "E63.trimOffspring", {"start": v(96.85, -31.13) * mm, "mid": v(98.26, -26.33) * mm, "end": v(99.44, -21.47) * mm});
            skLineSegment(sketch, "E64", {"start": v(25.68, -95.85) * mm, "end": v(20.85, -97.14) * mm, "construction": true});
            skLineSegment(sketch, "E65.MirrorCS", {"start": v(25.68, -95.85) * mm, "end": v(30.51, -94.55) * mm, "construction": true});
            skLineSegment(sketch, "E66", {"start": v(31.13, -96.85) * mm, "end": v(31.9, -99.75) * mm});
            skLineSegment(sketch, "E67", {"start": v(21.47, -99.44) * mm, "end": v(22.25, -102.34) * mm});
            skArc(sketch, "E68.trimOffspring", {"start": v(68.31, -75.38) * mm, "mid": v(71.93, -71.93) * mm, "end": v(75.38, -68.31) * mm});
            skArc(sketch, "E69.trimOffspring", {"start": v(70.44, -77.5) * mm, "mid": v(74.06, -74.06) * mm, "end": v(77.5, -70.44) * mm});
            skSolve(sketch);
        }
        {
            var Q0;
            Q0=makeQuery(id+"F15.imprint","IMPRINT",FACE,{"disambiguationData":[TD([[makeQuery(id+"F15.imprint","IMPRINT",EDGE,{"derivedFrom":sQuery(id+"F15.wireOp",EDGE,"E34")}),1.0]])]});
            var Q1;
            Q1=makeQuery(id+"F15.imprint","IMPRINT",FACE,{"disambiguationData":[TD([[makeQuery(id+"F15.imprint","IMPRINT",EDGE,{"derivedFrom":sQuery(id+"F15.wireOp",EDGE,"E60")}),-1.0]])]});
            var Q2;
            Q2=makeQuery(id+"F15.imprint","IMPRINT",FACE,{"disambiguationData":[TD([[makeQuery(id+"F15.imprint","IMPRINT",EDGE,{"derivedFrom":sQuery(id+"F15.wireOp",EDGE,"E54")}),1.0]])]});
            var Q3;
            Q3=makeQuery(id+"F15.imprint","IMPRINT",FACE,{"disambiguationData":[TD([[makeQuery(id+"F15.imprint","IMPRINT",EDGE,{"derivedFrom":sQuery(id+"F15.wireOp",EDGE,"E48")}),-1.0]])]});
            var Q4;
            Q4=makeQuery(id+"F15.imprint","IMPRINT",FACE,{"disambiguationData":[TD([[makeQuery(id+"F15.imprint","IMPRINT",EDGE,{"derivedFrom":sQuery(id+"F15.wireOp",EDGE,"E42")}),1.0]])]});
            var Q5;
            Q5=makeQuery(id+"F15.imprint","IMPRINT",FACE,{"disambiguationData":[TD([[makeQuery(id+"F15.imprint","IMPRINT",EDGE,{"derivedFrom":sQuery(id+"F15.wireOp",EDGE,"E38")}),-1.0]])]});
            extrude(context, id + "F16", {"entities" : qUnion([Q0, Q1, Q2, Q3, Q4, Q5]), "operationType" : NewBodyOperationType.ADD, "depth" : 5 * mm, "offsetDistance" : 25 * mm});
        }
        {
            var Q0;
            Q0=makeQuery(id+"F16.opExtrude","CAP_FACE",FACE,{"disambiguationData":[OSD([sQuery(id+"F15.wireOp",EDGE,"E34"),sQuery(id+"F15.wireOp",EDGE,"E35"),sQuery(id+"F15.wireOp",EDGE,"E66"),sQuery(id+"F15.wireOp",EDGE,"E67")])],"isStart":false});
            var sketch = newSketch(context, id + "F17", { "sketchPlane" : qUnion([Q0])});
            skLineSegment(sketch, "E70", {"start": v(27.24, -101.64) * mm, "end": v(26.2, -97.78) * mm});
            skLineSegment(sketch, "E71", {"start": v(26.2, -97.78) * mm, "end": v(27.17, -97.52) * mm});
            skLineSegment(sketch, "E72", {"start": v(27.17, -97.52) * mm, "end": v(28.2, -101.39) * mm});
            skLineSegment(sketch, "E73", {"start": v(28.2, -101.39) * mm, "end": v(27.24, -101.64) * mm});
            skLineSegment(sketch, "E74.1.0", {"start": v(75.12, -73.7) * mm, "end": v(74.4, -74.4) * mm});
            skLineSegment(sketch, "E74.1.1", {"start": v(72.29, -70.87) * mm, "end": v(75.12, -73.7) * mm});
            skLineSegment(sketch, "E74.1.2", {"start": v(71.58, -71.58) * mm, "end": v(72.29, -70.87) * mm});
            skLineSegment(sketch, "E74.1.3", {"start": v(74.4, -74.4) * mm, "end": v(71.58, -71.58) * mm});
            skLineSegment(sketch, "E74.2.0", {"start": v(101.9, -26.27) * mm, "end": v(101.64, -27.24) * mm});
            skLineSegment(sketch, "E74.2.1", {"start": v(98.04, -25.23) * mm, "end": v(101.9, -26.27) * mm});
            skLineSegment(sketch, "E74.2.2", {"start": v(97.78, -26.2) * mm, "end": v(98.04, -25.23) * mm});
            skLineSegment(sketch, "E74.2.3", {"start": v(101.64, -27.24) * mm, "end": v(97.78, -26.2) * mm});
            skLineSegment(sketch, "E74.3.0", {"start": v(101.39, 28.2) * mm, "end": v(101.64, 27.24) * mm});
            skLineSegment(sketch, "E74.3.1", {"start": v(97.52, 27.17) * mm, "end": v(101.39, 28.2) * mm});
            skLineSegment(sketch, "E74.3.2", {"start": v(97.78, 26.2) * mm, "end": v(97.52, 27.17) * mm});
            skLineSegment(sketch, "E74.3.3", {"start": v(101.64, 27.24) * mm, "end": v(97.78, 26.2) * mm});
            skLineSegment(sketch, "E74.4.0", {"start": v(73.7, 75.12) * mm, "end": v(74.4, 74.4) * mm});
            skLineSegment(sketch, "E74.4.1", {"start": v(70.87, 72.29) * mm, "end": v(73.7, 75.12) * mm});
            skLineSegment(sketch, "E74.4.2", {"start": v(71.58, 71.58) * mm, "end": v(70.87, 72.29) * mm});
            skLineSegment(sketch, "E74.4.3", {"start": v(74.4, 74.4) * mm, "end": v(71.58, 71.58) * mm});
            skLineSegment(sketch, "E74.5.0", {"start": v(26.27, 101.9) * mm, "end": v(27.24, 101.64) * mm});
            skLineSegment(sketch, "E74.5.1", {"start": v(25.23, 98.04) * mm, "end": v(26.27, 101.9) * mm});
            skLineSegment(sketch, "E74.5.2", {"start": v(26.2, 97.78) * mm, "end": v(25.23, 98.04) * mm});
            skLineSegment(sketch, "E74.5.3", {"start": v(27.24, 101.64) * mm, "end": v(26.2, 97.78) * mm});
            skLineSegment(sketch, "E74.6.0", {"start": v(-28.2, 101.39) * mm, "end": v(-27.24, 101.64) * mm});
            skLineSegment(sketch, "E74.6.1", {"start": v(-27.17, 97.52) * mm, "end": v(-28.2, 101.39) * mm});
            skLineSegment(sketch, "E74.6.2", {"start": v(-26.2, 97.78) * mm, "end": v(-27.17, 97.52) * mm});
            skLineSegment(sketch, "E74.6.3", {"start": v(-27.24, 101.64) * mm, "end": v(-26.2, 97.78) * mm});
            skLineSegment(sketch, "E74.7.0", {"start": v(-75.12, 73.7) * mm, "end": v(-74.4, 74.4) * mm});
            skLineSegment(sketch, "E74.7.1", {"start": v(-72.29, 70.87) * mm, "end": v(-75.12, 73.7) * mm});
            skLineSegment(sketch, "E74.7.2", {"start": v(-71.58, 71.58) * mm, "end": v(-72.29, 70.87) * mm});
            skLineSegment(sketch, "E74.7.3", {"start": v(-74.4, 74.4) * mm, "end": v(-71.58, 71.58) * mm});
            skLineSegment(sketch, "E74.8.0", {"start": v(-101.9, 26.27) * mm, "end": v(-101.64, 27.24) * mm});
            skLineSegment(sketch, "E74.8.1", {"start": v(-98.04, 25.23) * mm, "end": v(-101.9, 26.27) * mm});
            skLineSegment(sketch, "E74.8.2", {"start": v(-97.78, 26.2) * mm, "end": v(-98.04, 25.23) * mm});
            skLineSegment(sketch, "E74.8.3", {"start": v(-101.64, 27.24) * mm, "end": v(-97.78, 26.2) * mm});
            skLineSegment(sketch, "E74.9.0", {"start": v(-101.39, -28.2) * mm, "end": v(-101.64, -27.24) * mm});
            skLineSegment(sketch, "E74.9.1", {"start": v(-97.52, -27.17) * mm, "end": v(-101.39, -28.2) * mm});
            skLineSegment(sketch, "E74.9.2", {"start": v(-97.78, -26.2) * mm, "end": v(-97.52, -27.17) * mm});
            skLineSegment(sketch, "E74.9.3", {"start": v(-101.64, -27.24) * mm, "end": v(-97.78, -26.2) * mm});
            skLineSegment(sketch, "E74.10.0", {"start": v(-73.7, -75.12) * mm, "end": v(-74.4, -74.4) * mm});
            skLineSegment(sketch, "E74.10.1", {"start": v(-70.87, -72.29) * mm, "end": v(-73.7, -75.12) * mm});
            skLineSegment(sketch, "E74.10.2", {"start": v(-71.58, -71.58) * mm, "end": v(-70.87, -72.29) * mm});
            skLineSegment(sketch, "E74.10.3", {"start": v(-74.4, -74.4) * mm, "end": v(-71.58, -71.58) * mm});
            skLineSegment(sketch, "E74.11.0", {"start": v(-26.27, -101.9) * mm, "end": v(-27.24, -101.64) * mm});
            skLineSegment(sketch, "E74.11.1", {"start": v(-25.23, -98.04) * mm, "end": v(-26.27, -101.9) * mm});
            skLineSegment(sketch, "E74.11.2", {"start": v(-26.2, -97.78) * mm, "end": v(-25.23, -98.04) * mm});
            skLineSegment(sketch, "E74.11.3", {"start": v(-27.24, -101.64) * mm, "end": v(-26.2, -97.78) * mm});
            skPoint(sketch, "E74.center", {"position": v(0, 0) * mm});
            skSolve(sketch);
        }
        {
            var Q0;
            {var subQ5=makeQuery(id+"F16.opExtrude","CAP_EDGE",EDGE,{"disambiguationData":[OSD([sQuery(id+"F15.wireOp",EDGE,"E66")])],"isStart":false});Q0=makeQuery(id+"F17.imprint","IMPRINT",FACE,{"disambiguationData":[TD([[makeQuery(id+"F17.imprint","IMPRINT",EDGE,{"derivedFrom":subQ5}),-1.0]])]});}
            var Q1;
            {var subQ0=sQuery(id+"F17.wireOp",EDGE,"E70");var subQ1=makeQuery(id+"F16.opExtrude","CAP_EDGE",EDGE,{"disambiguationData":[OSD([sQuery(id+"F15.wireOp",EDGE,"E34")])],"isStart":false});var subQ2=makeQuery(id+"F17.imprint","INTERSECT",VERTEX,{"derivedFrom":[subQ1,subQ0]});Q1=makeQuery(id+"F17.imprint","IMPRINT",FACE,{"disambiguationData":[TD([[makeQuery(id+"F17.imprint","IMPRINT",EDGE,{"disambiguationData":[TD([[subQ2,-1.0]])],"derivedFrom":subQ0}),-1.0]])]});}
            var Q2;
            {var subQ5=makeQuery(id+"F16.opExtrude","CAP_EDGE",EDGE,{"disambiguationData":[OSD([sQuery(id+"F15.wireOp",EDGE,"E67")])],"isStart":false});Q2=makeQuery(id+"F17.imprint","IMPRINT",FACE,{"disambiguationData":[TD([[makeQuery(id+"F17.imprint","IMPRINT",EDGE,{"derivedFrom":subQ5}),1.0]])]});}
            extrude(context, id + "F18", {"entities" : qUnion([Q0, Q1, Q2]), "operationType" : NewBodyOperationType.ADD, "depth" : 5 * mm, "offsetDistance" : 25 * mm});
        }
        {
            var Q0;
            Q0=makeQuery(id+"F16.opExtrude","CAP_FACE",FACE,{"disambiguationData":[OSD([sQuery(id+"F15.wireOp",EDGE,"E60"),sQuery(id+"F15.wireOp",EDGE,"E61"),sQuery(id+"F15.wireOp",EDGE,"E68.trimOffspring"),sQuery(id+"F15.wireOp",EDGE,"E69.trimOffspring")])],"isStart":false});
            extrude(context, id + "F19", {"entities" : qUnion([Q0]), "operationType" : NewBodyOperationType.ADD, "depth" : 5 * mm, "offsetDistance" : 25 * mm});
        }
        {
            var Q0;
            Q0=makeQuery(id+"F16.opExtrude","CAP_FACE",FACE,{"disambiguationData":[OSD([sQuery(id+"F15.wireOp",EDGE,"E54"),sQuery(id+"F15.wireOp",EDGE,"E55"),sQuery(id+"F15.wireOp",EDGE,"E62.trimOffspring"),sQuery(id+"F15.wireOp",EDGE,"E63.trimOffspring")])],"isStart":false});
            extrude(context, id + "F20", {"entities" : qUnion([Q0]), "operationType" : NewBodyOperationType.ADD, "depth" : 5 * mm, "offsetDistance" : 25 * mm});
        }
        {
            var Q0;
            Q0=makeQuery(id+"F16.opExtrude","CAP_FACE",FACE,{"disambiguationData":[OSD([sQuery(id+"F15.wireOp",EDGE,"E48"),sQuery(id+"F15.wireOp",EDGE,"E49"),sQuery(id+"F15.wireOp",EDGE,"E56.trimOffspring"),sQuery(id+"F15.wireOp",EDGE,"E57.trimOffspring")])],"isStart":false});
            extrude(context, id + "F21", {"entities" : qUnion([Q0]), "operationType" : NewBodyOperationType.ADD, "depth" : 5 * mm, "offsetDistance" : 25 * mm});
        }
        {
            var Q0;
            Q0=makeQuery(id+"F16.opExtrude","CAP_FACE",FACE,{"disambiguationData":[OSD([sQuery(id+"F15.wireOp",EDGE,"E42"),sQuery(id+"F15.wireOp",EDGE,"E43"),sQuery(id+"F15.wireOp",EDGE,"E50.trimOffspring"),sQuery(id+"F15.wireOp",EDGE,"E51.trimOffspring")])],"isStart":false});
            extrude(context, id + "F22", {"entities" : qUnion([Q0]), "operationType" : NewBodyOperationType.ADD, "depth" : 5 * mm, "offsetDistance" : 25 * mm});
        }
        {
            var Q0;
            Q0=makeQuery(id+"F16.opExtrude","CAP_FACE",FACE,{"disambiguationData":[OSD([sQuery(id+"F15.wireOp",EDGE,"E38"),sQuery(id+"F15.wireOp",EDGE,"E39"),sQuery(id+"F15.wireOp",EDGE,"E44.trimOffspring"),sQuery(id+"F15.wireOp",EDGE,"E45.trimOffspring")])],"isStart":false});
            extrude(context, id + "F23", {"entities" : qUnion([Q0]), "operationType" : NewBodyOperationType.ADD, "depth" : 5 * mm, "offsetDistance" : 25 * mm});
        }
        {
            var Q0;
            Q0=makeQuery(id+"F17.imprint","IMPRINT",FACE,{"disambiguationData":[TD([[makeQuery(id+"F17.imprint","IMPRINT",EDGE,{"derivedFrom":sQuery(id+"F17.wireOp",EDGE,"E74.5.0")}),-1.0]])]});
            var Q1;
            Q1=sQuery(id+"F17.wireOp",EDGE,"E74.5.3");
            revolve(context, id + "F24", {"operationType" : NewBodyOperationType.REMOVE, "surfaceOperationType" : NewSurfaceOperationType.NEW, "entities" : qUnion([Q0]), "axis" : qUnion([Q1]), "revolveType" : RevolveType.FULL, "oppositeDirection" : true});
        }
        {
            var Q0;
            Q0=makeQuery(id+"F17.imprint","IMPRINT",FACE,{"disambiguationData":[TD([[makeQuery(id+"F17.imprint","IMPRINT",EDGE,{"derivedFrom":sQuery(id+"F17.wireOp",EDGE,"E74.4.0")}),-1.0]])]});
            var Q1;
            Q1=sQuery(id+"F17.wireOp",EDGE,"E74.4.3");
            revolve(context, id + "F25", {"operationType" : NewBodyOperationType.REMOVE, "surfaceOperationType" : NewSurfaceOperationType.NEW, "entities" : qUnion([Q0]), "axis" : qUnion([Q1]), "revolveType" : RevolveType.FULL, "oppositeDirection" : true});
        }
        {
            var Q0;
            Q0=makeQuery(id+"F17.imprint","IMPRINT",FACE,{"disambiguationData":[TD([[makeQuery(id+"F17.imprint","IMPRINT",EDGE,{"derivedFrom":sQuery(id+"F17.wireOp",EDGE,"E74.3.0")}),-1.0]])]});
            var Q1;
            Q1=sQuery(id+"F17.wireOp",EDGE,"E74.3.3");
            revolve(context, id + "F26", {"operationType" : NewBodyOperationType.REMOVE, "surfaceOperationType" : NewSurfaceOperationType.NEW, "entities" : qUnion([Q0]), "axis" : qUnion([Q1]), "revolveType" : RevolveType.FULL, "oppositeDirection" : true});
        }
        {
            var Q0;
            Q0=makeQuery(id+"F17.imprint","IMPRINT",FACE,{"disambiguationData":[TD([[makeQuery(id+"F17.imprint","IMPRINT",EDGE,{"derivedFrom":sQuery(id+"F17.wireOp",EDGE,"E74.2.0")}),-1.0]])]});
            var Q1;
            Q1=sQuery(id+"F17.wireOp",EDGE,"E74.2.3");
            revolve(context, id + "F27", {"operationType" : NewBodyOperationType.REMOVE, "surfaceOperationType" : NewSurfaceOperationType.NEW, "entities" : qUnion([Q0]), "axis" : qUnion([Q1]), "revolveType" : RevolveType.FULL, "oppositeDirection" : true});
        }
        {
            var Q0;
            Q0=makeQuery(id+"F17.imprint","IMPRINT",FACE,{"disambiguationData":[TD([[makeQuery(id+"F17.imprint","IMPRINT",EDGE,{"derivedFrom":sQuery(id+"F17.wireOp",EDGE,"E74.1.0")}),-1.0]])]});
            var Q1;
            Q1=sQuery(id+"F17.wireOp",EDGE,"E74.1.3");
            revolve(context, id + "F28", {"operationType" : NewBodyOperationType.REMOVE, "surfaceOperationType" : NewSurfaceOperationType.NEW, "entities" : qUnion([Q0]), "axis" : qUnion([Q1]), "revolveType" : RevolveType.FULL, "oppositeDirection" : true});
        }
        {
            var Q0;
            {var subQ0=sQuery(id+"F17.wireOp",EDGE,"E73");Q0=makeQuery(id+"F17.imprint","IMPRINT",FACE,{"disambiguationData":[TD([[makeQuery(id+"F17.imprint","IMPRINT",EDGE,{"derivedFrom":subQ0}),-1.0]])]});}
            var Q1;
            {var subQ0=sQuery(id+"F17.wireOp",EDGE,"E71");Q1=makeQuery(id+"F17.imprint","IMPRINT",FACE,{"disambiguationData":[TD([[makeQuery(id+"F17.imprint","IMPRINT",EDGE,{"derivedFrom":subQ0}),-1.0]])]});}
            var Q2;
            {var subQ0=sQuery(id+"F17.wireOp",EDGE,"E70");var subQ1=makeQuery(id+"F16.opExtrude","CAP_EDGE",EDGE,{"disambiguationData":[OSD([sQuery(id+"F15.wireOp",EDGE,"E34")])],"isStart":false});var subQ2=makeQuery(id+"F17.imprint","INTERSECT",VERTEX,{"derivedFrom":[subQ1,subQ0]});Q2=makeQuery(id+"F17.imprint","IMPRINT",FACE,{"disambiguationData":[TD([[makeQuery(id+"F17.imprint","IMPRINT",EDGE,{"disambiguationData":[TD([[subQ2,-1.0]])],"derivedFrom":subQ0}),-1.0]])]});}
            var Q3;
            Q3=sQuery(id+"F17.wireOp",EDGE,"E70");
            revolve(context, id + "F29", {"operationType" : NewBodyOperationType.REMOVE, "surfaceOperationType" : NewSurfaceOperationType.NEW, "entities" : qUnion([Q0, Q1, Q2]), "axis" : qUnion([Q3]), "revolveType" : RevolveType.FULL, "oppositeDirection" : true});
        }
    });
